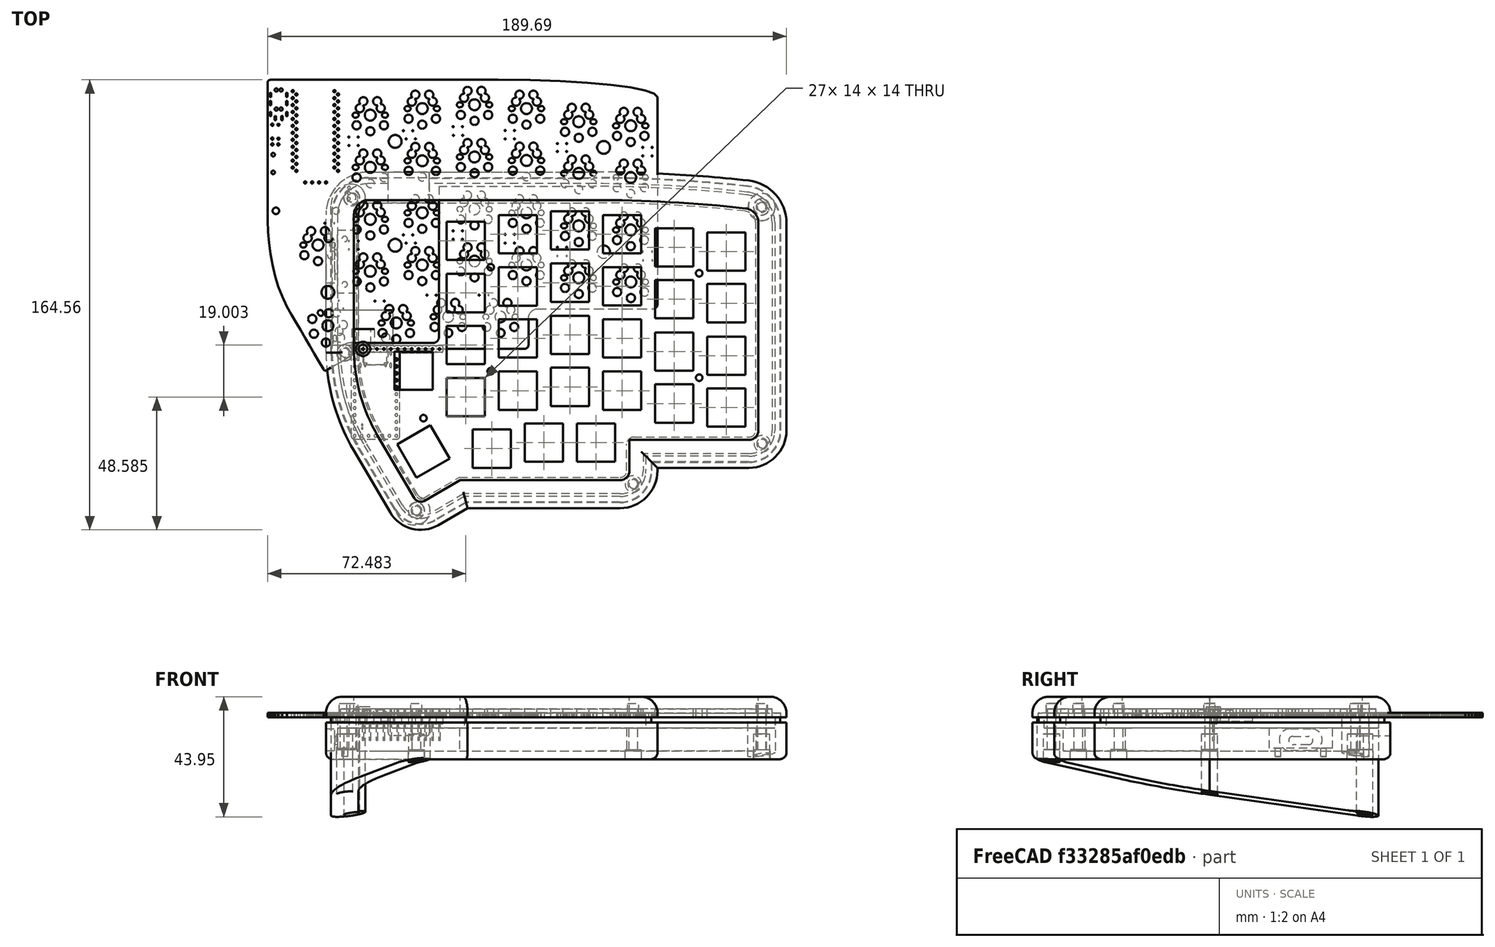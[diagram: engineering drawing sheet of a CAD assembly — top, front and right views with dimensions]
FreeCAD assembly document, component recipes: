
FREECAD ASSEMBLY — COMPONENT RECIPES ("pro_case_usbc_gasket_mount")

This assembly document has 10 components, labeled P0..P9 below (a component is one placed body or linked part). 8 of them carry a construction recipe — the FreeCAD feature program that regenerates the part from scratch, quoted from this document or its linked companion documents; the rest are supplied as boundary geometry only. No exploded tour is included for this assembly.
COMPONENT P0 — geometry summary ("Assembly"; no construction recipe available for this part):
  bounding box: 168.3 x 130.9 x 57.9 mm
  tessellated surface: 6,794 triangles
  volume: 358568995028408542041603690275402591667296508010351050356882624388695640748972656916483938942223122432 mm^3 (28139869802548311578441350783873821264969144354978867066293257606694140065651820190811947033165824% of its bounding box)
COMPONENT P1 — geometry summary ("lily58_pcb"; no construction recipe available for this part):
  bounding box: 142.5 x 106.3 x 1.6 mm
  tessellated surface: 11,472 triangles
  volume: 17508 mm^3 (72% of its bounding box)
  symmetry: mirror-symmetric across its z mid-plane
COMPONENT P2 — recipe-attached ("top_plate", modeled in this document).
Construction recipe (the document's own serialized feature program — sketch geometry with constraints, then the solid features built on it; lengths are millimeters unless a unit is written):

FEATURE [PartDesign::ShapeBinder] ShapeBinder002
  Placement = pos=(-82.9363,87.5957,1.6) rot=(0,0,1;0rad)
  Support = -> [Board_outline]
  TraceSupport = false
FEATURE [Sketcher::SketchObject] Sketch008  label="s_top_plate001"
  ExternalGeometry = -> [ShapeBinder002]
  FullyConstrained = true
  MapMode = 5
  Support = -> [XY_Plane010]
  expr: Constraints[435] = <<ss_top_plate>>.screw_hole_od
  expr: Constraints[85] = <<ss_top_plate>>.gasket_width
  sketch-geometry (187):
    g0: LineSegment StartX=27.7441 StartY=2.20222 StartZ=0 EndX=27.7441 EndY=50.2465 EndZ=0
    g1: LineSegment StartX=29.9578 StartY=52.4601 StartZ=0 EndX=84.3125 EndY=52.4601 EndZ=0
    g2: LineSegment StartX=142.522 StartY=46.1101 StartZ=0 EndX=142.522 EndY=-29.7428 EndZ=0
    g3: LineSegment StartX=95.381 StartY=-34.7428 StartZ=0 EndX=95.381 EndY=-44.4872 EndZ=0
    g4: LineSegment StartX=93.9034 StartY=-45.9648 StartZ=0 EndX=34.9248 EndY=-45.9648 EndZ=0
    g5: LineSegment StartX=34.9248 StartY=-45.9648 StartZ=0 EndX=21.3774 EndY=-53.8065 EndZ=0
    g6: LineSegment StartX=20.5079 StartY=-53.5776 StartZ=0 EndX=7.05497 EndY=-30.6854 EndZ=0
    g7: LineSegment StartX=98.881 StartY=-31.2428 StartZ=0 EndX=141.022 EndY=-31.2428 EndZ=0
    g8: LineSegment StartX=27.7441 StartY=2.20222 StartZ=0 EndX=2.19941 EndY=2.20233 EndZ=0
    g9: ArcOfCircle CenterX=59.4385 CenterY=0.0985715 CenterZ=0 NormalX=0 NormalY=0 NormalZ=1 AngleXU=0 Radius=60.7592 StartAngle=3.16603 EndAngle=3.67289
    g10: ArcOfCircle CenterX=2.19939 CenterY=-1.30071 CenterZ=0 NormalX=0 NormalY=0 NormalZ=1 AngleXU=0 Radius=3.50304 StartAngle=1.57079 EndAngle=3.16603
    g11: ArcOfCircle CenterX=84.3125 CenterY=-450.952 CenterZ=0 NormalX=0 NormalY=0 NormalZ=1 AngleXU=0 Radius=503.412 StartAngle=1.46083 EndAngle=1.5708
    g12: ArcOfCircle CenterX=139.192 CenterY=46.1101 CenterZ=0 NormalX=0 NormalY=0 NormalZ=1 AngleXU=0 Radius=3.32961 StartAngle=6e-16 EndAngle=1.46083
    g13: ArcOfCircle CenterX=21.0579 CenterY=-53.2544 CenterZ=0 NormalX=0 NormalY=0 NormalZ=1 AngleXU=0 Radius=0.637877 StartAngle=3.67289 EndAngle=5.2371
    g14: ArcOfCircle CenterX=93.9034 CenterY=-44.4872 CenterZ=0 NormalX=0 NormalY=0 NormalZ=1 AngleXU=0 Radius=1.47761 StartAngle=4.71239 EndAngle=6.28319
    g15: ArcOfCircle CenterX=98.881 CenterY=-34.7428 CenterZ=0 NormalX=0 NormalY=0 NormalZ=1 AngleXU=0 Radius=3.5 StartAngle=1.5708 EndAngle=3.14159
    g16: ArcOfCircle CenterX=141.022 CenterY=-29.7428 CenterZ=0 NormalX=0 NormalY=0 NormalZ=1 AngleXU=0 Radius=1.5 StartAngle=4.71239 EndAngle=6.28319
    g17: ArcOfCircle CenterX=29.9578 CenterY=50.2465 CenterZ=0 NormalX=0 NormalY=0 NormalZ=1 AngleXU=0 Radius=2.21364 StartAngle=1.5708 EndAngle=3.14159
    g18: LineSegment StartX=-1.3026 StartY=-1.38632 StartZ=0 EndX=0.0777 EndY=-1.38632 EndZ=0
    g19: LineSegment StartX=27.7344 StartY=59.4601 StartZ=0 EndX=84.3125 EndY=59.4601 EndZ=0
    g20: LineSegment StartX=149.522 StartY=46.1101 StartZ=0 EndX=149.522 EndY=-29.7428 EndZ=0
    g21: LineSegment StartX=141.022 StartY=-38.2428 StartZ=0 EndX=102.381 EndY=-38.2428 EndZ=0
    g22: LineSegment StartX=102.381 StartY=-38.2428 StartZ=0 EndX=102.381 EndY=-44.4872 EndZ=0
    g23: LineSegment StartX=93.9034 StartY=-52.9648 StartZ=0 EndX=36.8046 EndY=-52.9648 EndZ=0
    g24: LineSegment StartX=36.8046 StartY=-52.9648 StartZ=0 EndX=24.8842 EndY=-59.8648 EndZ=0
    g25: LineSegment StartX=14.4729 StartY=-57.1242 StartZ=0 EndX=1.01993 EndY=-34.232 EndZ=0
    g26: ArcOfCircle CenterX=139.192 CenterY=46.1101 CenterZ=0 NormalX=0 NormalY=0 NormalZ=1 AngleXU=0 Radius=10.3296 StartAngle=0 EndAngle=1.46083
    g27: ArcOfCircle CenterX=84.3125 CenterY=-450.952 CenterZ=0 NormalX=0 NormalY=0 NormalZ=1 AngleXU=0 Radius=510.412 StartAngle=1.46083 EndAngle=1.5708
    g28: ArcOfCircle CenterX=59.4385 CenterY=0.0985715 CenterZ=0 NormalX=0 NormalY=0 NormalZ=1 AngleXU=0 Radius=67.7592 StartAngle=3.16351 EndAngle=3.67289
    g29: ArcOfCircle CenterX=21.0579 CenterY=-53.2544 CenterZ=0 NormalX=0 NormalY=0 NormalZ=1 AngleXU=0 Radius=7.63788 StartAngle=3.67289 EndAngle=5.2371
    g30: ArcOfCircle CenterX=93.9034 CenterY=-44.4872 CenterZ=0 NormalX=0 NormalY=0 NormalZ=1 AngleXU=0 Radius=8.47761 StartAngle=4.71239 EndAngle=6.28319
    g31: ArcOfCircle CenterX=141.022 CenterY=-29.7428 CenterZ=0 NormalX=0 NormalY=0 NormalZ=1 AngleXU=0 Radius=8.5 StartAngle=4.71239 EndAngle=6.28319
    g32: LineSegment StartX=141.022 StartY=-38.2428 StartZ=0 EndX=141.022 EndY=-31.2428 EndZ=0
    g33: LineSegment StartX=93.9034 StartY=-52.9648 StartZ=0 EndX=93.9034 EndY=-45.9648 EndZ=0
    g34: LineSegment StartX=24.8842 StartY=-59.8648 StartZ=0 EndX=21.3774 EndY=-53.8065 EndZ=0
    g35: LineSegment StartX=1.01993 StartY=-34.232 StartZ=0 EndX=7.05497 EndY=-30.6854 EndZ=0
    g36: LineSegment StartX=27.7344 StartY=59.4601 StartZ=0 EndX=27.7441 EndY=4.40223 EndZ=0
    g37: LineSegment StartX=25.5445 StartY=2.20223 StartZ=0 EndX=-4.79372 EndY=2.20223 EndZ=0
    g38: ArcOfCircle CenterX=-4.79372 CenterY=-1.30937 CenterZ=0 NormalX=0 NormalY=0 NormalZ=1 AngleXU=0 Radius=3.5116 StartAngle=1.5708 EndAngle=3.16351
    g39: ArcOfCircle CenterX=25.5445 CenterY=4.40184 CenterZ=0 NormalX=0 NormalY=0 NormalZ=1 AngleXU=0 Radius=2.19961 StartAngle=4.71239 EndAngle=6.28336
    g40: LineSegment StartX=84.3125 StartY=52.4601 StartZ=0 EndX=84.3125 EndY=59.4601 EndZ=0
    g41: LineSegment StartX=11.463 StartY=-0.95364 StartZ=0 EndX=25.4152 EndY=-0.95364 EndZ=0
    g42: LineSegment StartX=25.4152 StartY=-0.95364 StartZ=0 EndX=25.4152 EndY=-14.9537 EndZ=0
    g43: LineSegment StartX=25.4152 StartY=-14.9537 StartZ=0 EndX=11.463 EndY=-14.9537 EndZ=0
    g44: LineSegment StartX=11.463 StartY=-14.9537 StartZ=0 EndX=11.463 EndY=-0.95364 EndZ=0
    g45: LineSegment StartX=30.5626 StartY=46.5466 StartZ=0 EndX=44.5628 EndY=46.5466 EndZ=0
    g46: LineSegment StartX=44.5628 StartY=46.5466 StartZ=0 EndX=44.5628 EndY=32.5466 EndZ=0
    g47: LineSegment StartX=44.5628 StartY=32.5466 StartZ=0 EndX=30.5626 EndY=32.5466 EndZ=0
    g48: LineSegment StartX=30.5626 StartY=32.5466 StartZ=0 EndX=30.5626 EndY=46.5466 EndZ=0
    g49: LineSegment StartX=49.5629 StartY=48.9469 StartZ=0 EndX=63.5631 EndY=48.9469 EndZ=0
    g50: LineSegment StartX=63.5631 StartY=48.9469 StartZ=0 EndX=63.5631 EndY=34.9469 EndZ=0
    g51: LineSegment StartX=63.5631 StartY=34.9469 StartZ=0 EndX=49.5629 EndY=34.9469 EndZ=0
    g52: LineSegment StartX=49.5629 StartY=34.9469 StartZ=0 EndX=49.5629 EndY=48.9469 EndZ=0
    g53: LineSegment StartX=68.5928 StartY=50.3363 StartZ=0 EndX=82.593 EndY=50.3363 EndZ=0
    g54: LineSegment StartX=82.593 StartY=50.3363 StartZ=0 EndX=82.593 EndY=36.3362 EndZ=0
    g55: LineSegment StartX=82.593 StartY=36.3362 StartZ=0 EndX=68.5928 EndY=36.3362 EndZ=0
    g56: LineSegment StartX=68.5928 StartY=36.3362 StartZ=0 EndX=68.5928 EndY=50.3363 EndZ=0
    g57: LineSegment StartX=87.6676 StartY=48.9469 StartZ=0 EndX=101.668 EndY=48.9469 EndZ=0
    g58: LineSegment StartX=101.668 StartY=48.9469 StartZ=0 EndX=101.668 EndY=34.9469 EndZ=0
    g59: LineSegment StartX=101.668 StartY=34.9469 StartZ=0 EndX=87.6676 EndY=34.9469 EndZ=0
    g60: LineSegment StartX=87.6676 StartY=34.9469 StartZ=0 EndX=87.6676 EndY=48.9469 EndZ=0
    g61: LineSegment StartX=106.764 StartY=44.1463 StartZ=0 EndX=120.764 EndY=44.1463 EndZ=0
    g62: LineSegment StartX=120.764 StartY=44.1463 StartZ=0 EndX=120.764 EndY=30.1463 EndZ=0
    g63: LineSegment StartX=120.764 StartY=30.1463 StartZ=0 EndX=106.764 EndY=30.1463 EndZ=0
    g64: LineSegment StartX=106.764 StartY=30.1463 StartZ=0 EndX=106.764 EndY=44.1463 EndZ=0
    g65: LineSegment StartX=125.761 StartY=42.6469 StartZ=0 EndX=139.762 EndY=42.6469 EndZ=0
    g66: LineSegment StartX=139.762 StartY=42.6469 StartZ=0 EndX=139.762 EndY=28.6464 EndZ=0
    g67: LineSegment StartX=139.762 StartY=28.6464 StartZ=0 EndX=125.761 EndY=28.6464 EndZ=0
    g68: LineSegment StartX=125.761 StartY=28.6464 StartZ=0 EndX=125.761 EndY=42.6469 EndZ=0
    g69: LineSegment StartX=30.5636 StartY=27.4453 StartZ=0 EndX=44.5638 EndY=27.4453 EndZ=0
    g70: LineSegment StartX=44.5638 StartY=27.4453 StartZ=0 EndX=44.5638 EndY=13.4453 EndZ=0
    g71: LineSegment StartX=44.5638 StartY=13.4453 StartZ=0 EndX=30.5636 EndY=13.4453 EndZ=0
    g72: LineSegment StartX=30.5636 StartY=13.4453 StartZ=0 EndX=30.5636 EndY=27.4453 EndZ=0
    g73: LineSegment StartX=49.5629 StartY=29.8461 StartZ=0 EndX=63.5631 EndY=29.8461 EndZ=0
    g74: LineSegment StartX=63.5631 StartY=29.8461 StartZ=0 EndX=63.5631 EndY=15.8461 EndZ=0
    g75: LineSegment StartX=63.5631 StartY=15.8461 StartZ=0 EndX=49.5629 EndY=15.8461 EndZ=0
    g76: LineSegment StartX=49.5629 StartY=15.8461 StartZ=0 EndX=49.5629 EndY=29.8461 EndZ=0
    g77: LineSegment StartX=68.6637 StartY=31.2457 StartZ=0 EndX=82.6639 EndY=31.2457 EndZ=0
    g78: LineSegment StartX=82.6639 StartY=31.2457 StartZ=0 EndX=82.6639 EndY=17.2456 EndZ=0
    g79: LineSegment StartX=82.6639 StartY=17.2456 StartZ=0 EndX=68.6637 EndY=17.2456 EndZ=0
    g80: LineSegment StartX=68.6637 StartY=17.2456 StartZ=0 EndX=68.6637 EndY=31.2457 EndZ=0
    g81: LineSegment StartX=87.6617 StartY=29.9467 StartZ=0 EndX=101.662 EndY=29.9467 EndZ=0
    g82: LineSegment StartX=101.662 StartY=29.9467 StartZ=0 EndX=101.662 EndY=15.9466 EndZ=0
    g83: LineSegment StartX=101.662 StartY=15.9466 StartZ=0 EndX=87.6617 EndY=15.9466 EndZ=0
    g84: LineSegment StartX=87.6617 StartY=15.9466 StartZ=0 EndX=87.6617 EndY=29.9467 EndZ=0
    g85: LineSegment StartX=106.762 StartY=25.2462 StartZ=0 EndX=120.763 EndY=25.2462 EndZ=0
    g86: LineSegment StartX=120.763 StartY=25.2462 StartZ=0 EndX=120.763 EndY=11.2462 EndZ=0
    g87: LineSegment StartX=120.763 StartY=11.2462 StartZ=0 EndX=106.762 EndY=11.2462 EndZ=0
    g88: LineSegment StartX=106.762 StartY=11.2462 StartZ=0 EndX=106.762 EndY=25.2462 EndZ=0
    g89: LineSegment StartX=125.761 StartY=23.7455 StartZ=0 EndX=139.762 EndY=23.7455 EndZ=0
    g90: LineSegment StartX=139.762 StartY=23.7455 StartZ=0 EndX=139.762 EndY=9.74756 EndZ=0
    g91: LineSegment StartX=139.762 StartY=9.74756 StartZ=0 EndX=125.761 EndY=9.74756 EndZ=0
    g92: LineSegment StartX=125.761 StartY=9.74756 StartZ=0 EndX=125.761 EndY=23.7455 EndZ=0
    g93: LineSegment StartX=30.5626 StartY=8.44811 StartZ=0 EndX=44.5628 EndY=8.44811 EndZ=0
    g94: LineSegment StartX=44.5628 StartY=8.44811 StartZ=0 EndX=44.5628 EndY=-5.55192 EndZ=0
    g95: LineSegment StartX=44.5628 StartY=-5.55192 StartZ=0 EndX=30.5626 EndY=-5.55192 EndZ=0
    g96: LineSegment StartX=30.5626 StartY=-5.55192 StartZ=0 EndX=30.5626 EndY=8.44811 EndZ=0
    g97: LineSegment StartX=49.5638 StartY=10.8451 StartZ=0 EndX=63.564 EndY=10.8451 EndZ=0
    g98: LineSegment StartX=63.564 StartY=10.8451 StartZ=0 EndX=63.564 EndY=-3.15488 EndZ=0
    g99: LineSegment StartX=63.564 StartY=-3.15488 StartZ=0 EndX=49.5638 EndY=-3.15488 EndZ=0
    g100: LineSegment StartX=49.5638 StartY=-3.15488 StartZ=0 EndX=49.5638 EndY=10.8451 EndZ=0
    g101: LineSegment StartX=68.6637 StartY=12.1474 StartZ=0 EndX=82.6639 EndY=12.1474 EndZ=0
    g102: LineSegment StartX=82.6639 StartY=12.1474 StartZ=0 EndX=82.6639 EndY=-1.85258 EndZ=0
    g103: LineSegment StartX=82.6639 StartY=-1.85258 StartZ=0 EndX=68.6637 EndY=-1.85258 EndZ=0
    g104: LineSegment StartX=68.6637 StartY=-1.85258 StartZ=0 EndX=68.6637 EndY=12.1474 EndZ=0
    g105: LineSegment StartX=87.6637 StartY=10.8474 StartZ=0 EndX=101.664 EndY=10.8474 EndZ=0
    g106: LineSegment StartX=101.664 StartY=10.8474 StartZ=0 EndX=101.664 EndY=-3.15263 EndZ=0
    g107: LineSegment StartX=101.664 StartY=-3.15263 StartZ=0 EndX=87.6637 EndY=-3.15263 EndZ=0
    g108: LineSegment StartX=87.6637 StartY=-3.15263 StartZ=0 EndX=87.6637 EndY=10.8474 EndZ=0
    g109: LineSegment StartX=106.749 StartY=6.04637 StartZ=0 EndX=120.749 EndY=6.04637 EndZ=0
    g110: LineSegment StartX=120.749 StartY=6.04637 StartZ=0 EndX=120.749 EndY=-7.95365 EndZ=0
    g111: LineSegment StartX=120.749 StartY=-7.95365 StartZ=0 EndX=106.749 EndY=-7.95365 EndZ=0
    g112: LineSegment StartX=106.749 StartY=-7.95365 StartZ=0 EndX=106.749 EndY=6.04637 EndZ=0
    g113: LineSegment StartX=125.764 StartY=4.54519 StartZ=0 EndX=139.764 EndY=4.54519 EndZ=0
    g114: LineSegment StartX=139.764 StartY=4.54519 StartZ=0 EndX=139.764 EndY=-9.45483 EndZ=0
    g115: LineSegment StartX=139.764 StartY=-9.45483 StartZ=0 EndX=125.764 EndY=-9.45483 EndZ=0
    g116: LineSegment StartX=125.764 StartY=-9.45483 StartZ=0 EndX=125.764 EndY=4.54519 EndZ=0
    g117: LineSegment StartX=30.5626 StartY=-10.5548 StartZ=0 EndX=44.5628 EndY=-10.5548 EndZ=0
    g118: LineSegment StartX=44.5628 StartY=-10.5548 StartZ=0 EndX=44.5628 EndY=-24.5548 EndZ=0
    g119: LineSegment StartX=44.5628 StartY=-24.5548 StartZ=0 EndX=30.5626 EndY=-24.5548 EndZ=0
    g120: LineSegment StartX=30.5626 StartY=-24.5548 StartZ=0 EndX=30.5626 EndY=-10.5548 EndZ=0
    g121: LineSegment StartX=49.5638 StartY=-8.25337 StartZ=0 EndX=63.564 EndY=-8.25337 EndZ=0
    g122: LineSegment StartX=63.564 StartY=-8.25337 StartZ=0 EndX=63.564 EndY=-22.2534 EndZ=0
    g123: LineSegment StartX=63.564 StartY=-22.2534 StartZ=0 EndX=49.5638 EndY=-22.2534 EndZ=0
    g124: LineSegment StartX=49.5638 StartY=-22.2534 StartZ=0 EndX=49.5638 EndY=-8.25337 EndZ=0
    g125: LineSegment StartX=68.6625 StartY=-6.85278 StartZ=0 EndX=82.6627 EndY=-6.85278 EndZ=0
    g126: LineSegment StartX=82.6627 StartY=-6.85278 StartZ=0 EndX=82.6627 EndY=-20.8528 EndZ=0
    g127: LineSegment StartX=82.6627 StartY=-20.8528 StartZ=0 EndX=68.6625 EndY=-20.8528 EndZ=0
    g128: LineSegment StartX=68.6625 StartY=-20.8528 StartZ=0 EndX=68.6625 EndY=-6.85278 EndZ=0
    g129: LineSegment StartX=87.663 StartY=-8.25358 StartZ=0 EndX=101.663 EndY=-8.25358 EndZ=0
    g130: LineSegment StartX=101.663 StartY=-8.25358 StartZ=0 EndX=101.663 EndY=-22.2536 EndZ=0
    g131: LineSegment StartX=101.663 StartY=-22.2536 StartZ=0 EndX=87.663 EndY=-22.2536 EndZ=0
    g132: LineSegment StartX=87.663 StartY=-22.2536 StartZ=0 EndX=87.663 EndY=-8.25358 EndZ=0
    g133: LineSegment StartX=106.763 StartY=-12.9526 StartZ=0 EndX=120.764 EndY=-12.9526 EndZ=0
    g134: LineSegment StartX=120.764 StartY=-12.9526 StartZ=0 EndX=120.764 EndY=-26.9526 EndZ=0
    g135: LineSegment StartX=120.764 StartY=-26.9526 StartZ=0 EndX=106.763 EndY=-26.9526 EndZ=0
    g136: LineSegment StartX=106.763 StartY=-26.9526 StartZ=0 EndX=106.763 EndY=-12.9526 EndZ=0
    g137: LineSegment StartX=125.812 StartY=-14.4535 StartZ=0 EndX=139.813 EndY=-14.4535 EndZ=0
    g138: LineSegment StartX=139.813 StartY=-14.4535 StartZ=0 EndX=139.813 EndY=-28.4535 EndZ=0
    g139: LineSegment StartX=139.813 StartY=-28.4535 StartZ=0 EndX=125.812 EndY=-28.4535 EndZ=0
    g140: LineSegment StartX=125.812 StartY=-28.4535 StartZ=0 EndX=125.812 EndY=-14.4535 EndZ=0
    g141: LineSegment StartX=40.0622 StartY=-29.4536 StartZ=0 EndX=54.0624 EndY=-29.4536 EndZ=0
    g142: LineSegment StartX=54.0624 StartY=-29.4536 StartZ=0 EndX=54.0624 EndY=-43.4537 EndZ=0
    g143: LineSegment StartX=54.0624 StartY=-43.4537 StartZ=0 EndX=40.0622 EndY=-43.4537 EndZ=0
    g144: LineSegment StartX=40.0622 StartY=-43.4537 StartZ=0 EndX=40.0622 EndY=-29.4536 EndZ=0
    g145: LineSegment StartX=59.0628 StartY=-27.2032 StartZ=0 EndX=73.063 EndY=-27.2032 EndZ=0
    g146: LineSegment StartX=73.063 StartY=-27.2032 StartZ=0 EndX=73.063 EndY=-41.2032 EndZ=0
    g147: LineSegment StartX=73.063 StartY=-41.2032 StartZ=0 EndX=59.0628 EndY=-41.2032 EndZ=0
    g148: LineSegment StartX=59.0628 StartY=-41.2032 StartZ=0 EndX=59.0628 EndY=-27.2032 EndZ=0
    g149: LineSegment StartX=78.1633 StartY=-27.2043 StartZ=0 EndX=92.1637 EndY=-27.2043 EndZ=0
    g150: LineSegment StartX=92.1637 StartY=-27.2043 StartZ=0 EndX=92.1637 EndY=-41.2047 EndZ=0
    g151: LineSegment StartX=92.1637 StartY=-41.2047 StartZ=0 EndX=78.1633 EndY=-41.2047 EndZ=0
    g152: LineSegment StartX=78.1633 StartY=-41.2047 StartZ=0 EndX=78.1633 EndY=-27.2043 EndZ=0
    g153: LineSegment StartX=12.5009 StartY=-34.891 StartZ=0 EndX=24.6255 EndY=-27.8909 EndZ=0
    g154: LineSegment StartX=24.6255 StartY=-27.8909 StartZ=0 EndX=31.6255 EndY=-40.0153 EndZ=0
    g155: LineSegment StartX=31.6255 StartY=-40.0153 StartZ=0 EndX=19.501 EndY=-47.0154 EndZ=0
    g156: LineSegment StartX=19.501 StartY=-47.0154 StartZ=0 EndX=12.5009 EndY=-34.891 EndZ=0
    g157: Circle CenterX=46.6637 CenterY=29.8957 CenterZ=0 NormalX=0 NormalY=0 NormalZ=1 AngleXU=0 Radius=1.2
    g158: Circle CenterX=122.864 CenterY=27.6957 CenterZ=0 NormalX=0 NormalY=0 NormalZ=1 AngleXU=0 Radius=1.2
    g159: Circle CenterX=122.864 CenterY=-10.5043 CenterZ=0 NormalX=0 NormalY=0 NormalZ=1 AngleXU=0 Radius=1.2
    g160: Circle CenterX=46.6637 CenterY=-8.10427 CenterZ=0 NormalX=0 NormalY=0 NormalZ=1 AngleXU=0 Radius=1.2
    g161: Circle CenterX=22.0637 CenterY=-25.3043 CenterZ=0 NormalX=0 NormalY=0 NormalZ=1 AngleXU=0 Radius=1.2
    g162: Circle CenterX=145.695 CenterY=51.9344 CenterZ=0 NormalX=0 NormalY=0 NormalZ=1 AngleXU=0 Radius=1.6
    g163: Circle CenterX=145.901 CenterY=-34.6219 CenterZ=0 NormalX=0 NormalY=0 NormalZ=1 AngleXU=0 Radius=1.6
    g164: Circle CenterX=98.7666 CenterY=-49.3504 CenterZ=0 NormalX=0 NormalY=0 NormalZ=1 AngleXU=0 Radius=1.6
    g165: Circle CenterX=19.5209 CenterY=-59.0934 CenterZ=0 NormalX=0 NormalY=0 NormalZ=1 AngleXU=0 Radius=1.6
    g166: Circle CenterX=-6.70447 CenterY=-1.38632 CenterZ=0 NormalX=0 NormalY=0 NormalZ=1 AngleXU=0 Radius=1.6
    g167: LineSegment StartX=20.8955 StartY=-53.8713 StartZ=0 EndX=19.1136 EndY=-60.6407 EndZ=0
    g168: LineSegment StartX=19.1136 StartY=-60.6407 StartZ=0 EndX=24.8842 EndY=-59.8648 EndZ=0
    g169: LineSegment StartX=19.1136 StartY=-60.6407 StartZ=0 EndX=14.4729 EndY=-57.1242 EndZ=0
    g170: LineSegment StartX=20.5079 StartY=-53.5776 StartZ=0 EndX=20.8955 EndY=-53.8713 EndZ=0
    g171: LineSegment StartX=21.3774 StartY=-53.8065 StartZ=0 EndX=20.8955 EndY=-53.8713 EndZ=0
    g172: LineSegment StartX=94.9482 StartY=-45.532 StartZ=0 EndX=99.8979 EndY=-50.4817 EndZ=0
    g173: LineSegment StartX=94.9482 StartY=-45.532 StartZ=0 EndX=93.9034 EndY=-44.4872 EndZ=0
    g174: LineSegment StartX=93.9034 StartY=-52.9648 StartZ=0 EndX=99.8979 EndY=-50.4817 EndZ=0
    g175: LineSegment StartX=99.8979 StartY=-50.4817 StartZ=0 EndX=102.381 EndY=-44.4872 EndZ=0
    g176: LineSegment StartX=142.082 StartY=-30.8035 StartZ=0 EndX=147.032 EndY=-35.7533 EndZ=0
    g177: LineSegment StartX=141.022 StartY=-38.2428 StartZ=0 EndX=147.032 EndY=-35.7533 EndZ=0
    g178: LineSegment StartX=147.032 StartY=-35.7533 StartZ=0 EndX=149.522 EndY=-29.7428 EndZ=0
    g179: LineSegment StartX=141.022 StartY=-31.2428 StartZ=0 EndX=142.082 EndY=-30.8035 EndZ=0
    g180: LineSegment StartX=142.082 StartY=-30.8035 StartZ=0 EndX=142.522 EndY=-29.7428 EndZ=0
    g181: LineSegment StartX=141.672 StartY=48.3316 StartZ=0 EndX=146.887 EndY=53.0018 EndZ=0
    g182: LineSegment StartX=140.326 StartY=56.3773 StartZ=0 EndX=146.887 EndY=53.0018 EndZ=0
    g183: LineSegment StartX=146.887 StartY=53.0018 StartZ=0 EndX=149.522 EndY=46.1101 EndZ=0
    g184: LineSegment StartX=142.522 StartY=46.1101 StartZ=0 EndX=141.672 EndY=48.3316 EndZ=0
    g185: LineSegment StartX=141.672 StartY=48.3316 StartZ=0 EndX=139.557 EndY=49.4196 EndZ=0
    g186: LineSegment StartX=-1.3026 StartY=-1.38632 StartZ=0 EndX=-8.30447 EndY=-1.38632 EndZ=0
  constraints (448):
    c: Vertical(g0)
    c: Coincident(g1,g-3)
    c: Horizontal(g1)
    c: Vertical(g2)
    c: Coincident(g4,g-8)
    c: Coincident(g4,g5)
    c: Coincident(g6,g-9)
    c: PointOnObject(g-8,g5)
    c: PointOnObject(g-7,g4)
    c: Horizontal(g7)
    c: Coincident(g8,g0)
    c: Tangent(g9,g6) = 1.5708
    c: Tangent(g9,g10) = -1.5708
    c: Tangent(g8,g10) = -1.5708
    c: Tangent(g11,g1) = 1.5708
    c: PointOnObject(g-13,g11)
    c: Tangent(g11,g12) = -1.5708
    c: Tangent(g2,g12) = 1.5708
    c: Coincident(g2,g-4)
    c: Tangent(g5,g13) = 1.5708
    c: Tangent(g6,g13) = 1.5708
    c: Coincident(g6,g-9)
    c: Tangent(g4,g14) = 1.5708
    c: Tangent(g3,g14) = 1.5708
    c: Tangent(g3,g15) = -1.5708
    c: Tangent(g7,g15) = 1.5708
    c: Tangent(g7,g16) = -1.5708
    c: Tangent(g2,g16) = 1.5708
    c: Coincident(g7,g-5)
    c: Coincident(g3,g-6)
    c: Coincident(g3,g-6)
    c: Coincident(g8,g-10)
    c: Tangent(g0,g17) = 1.5708
    c: Tangent(g1,g17) = 1.5708
    c: Coincident(g0,g-11)
    c: Coincident(g18,g9)
    c: Coincident(g18,g-12)
    c: Horizontal(g18)
    c: Horizontal(g19)
    c: Vertical(g20)
    c: Horizontal(g21)
    c: Coincident(g21,g22)
    c: Vertical(g22)
    c: Horizontal(g23)
    c: Coincident(g23,g24)
    c: Coincident(g27,g11)
    c: Tangent(g27,g19) = 1.5708
    c: Tangent(g27,g26) = -1.5708
    c: Tangent(g26,g20) = 1.5708
    c: Coincident(g28,g9)
    c: Coincident(g28,g25)
    c: Tangent(g25,g29) = 1.5708
    c: Tangent(g24,g29) = 1.5708
    c: Tangent(g23,g30) = 1.5708
    c: Tangent(g22,g30) = 1.5708
    c: Tangent(g21,g31) = 1.5708
    c: Tangent(g20,g31) = 1.5708
    c: Coincident(g31,g16)
    c: Coincident(g26,g12)
    c: Coincident(g29,g13)
    c: Parallel(g24,g5)
    c: Parallel(g6,g25)
    c: Coincident(g30,g14)
    c: Coincident(g32,g21)
    c: Coincident(g32,g7)
    c: Coincident(g33,g23)
    c: Coincident(g33,g4)
    c: Coincident(g34,g24)
    c: Coincident(g34,g5)
    c: Coincident(g35,g25)
    c: Coincident(g35,g6)
    c: Perpendicular(g6,g35)
    c: Coincident(g36,g19)
    c: Horizontal(g37)
    c: Tangent(g28,g38) = -1.5708
    c: Tangent(g37,g38) = -1.5708
    c: Horizontal(g28,g9)
    c: Tangent(g36,g39) = 1.5708
    c: Tangent(g37,g39) = 1.5708
    c: Coincident(g37,g-10)
    c: Coincident(g36,g-11)
    c: Coincident(g40,g1)
    c: Coincident(g40,g19)
    c: Equal(g32,g33)
    c: Equal(g33,g34)
    c: DistanceY(g40,g40) = 7
    c: PointOnObject(g37,g8)
    c: Coincident(g41,g42)
    c: Coincident(g42,g43)
    c: Coincident(g43,g44)
    c: Coincident(g44,g41)
    c: Horizontal(g41)
    c: Horizontal(g43)
    c: Vertical(g42)
    c: Vertical(g44)
    c: Coincident(g41,g-16)
    c: Coincident(g42,g-17)
    c: Coincident(g45,g46)
    c: Coincident(g46,g47)
    c: Coincident(g47,g48)
    c: Coincident(g48,g45)
    c: Horizontal(g45)
    c: Horizontal(g47)
    c: Vertical(g46)
    c: Vertical(g48)
    c: Coincident(g45,g-18)
    c: Coincident(g46,g-19)
    c: Coincident(g49,g50)
    c: Coincident(g50,g51)
    c: Coincident(g51,g52)
    c: Coincident(g52,g49)
    c: Horizontal(g49)
    c: Horizontal(g51)
    c: Vertical(g50)
    c: Vertical(g52)
    c: Coincident(g49,g-20)
    c: Coincident(g50,g-21)
    c: Coincident(g53,g54)
    c: Coincident(g54,g55)
    c: Coincident(g55,g56)
    c: Coincident(g56,g53)
    c: Horizontal(g53)
    c: Horizontal(g55)
    c: Vertical(g54)
    c: Vertical(g56)
    c: Coincident(g53,g-22)
    c: Coincident(g54,g-23)
    c: Coincident(g57,g58)
    c: Coincident(g58,g59)
    c: Coincident(g59,g60)
    c: Coincident(g60,g57)
    c: Horizontal(g57)
    c: Horizontal(g59)
    c: Vertical(g58)
    c: Vertical(g60)
    c: Coincident(g57,g-24)
    c: Coincident(g58,g-25)
    c: Coincident(g61,g62)
    c: Coincident(g62,g63)
    c: Coincident(g63,g64)
    c: Coincident(g64,g61)
    c: Horizontal(g61)
    c: Horizontal(g63)
    c: Vertical(g62)
    c: Vertical(g64)
    c: Coincident(g61,g-26)
    c: Coincident(g62,g-27)
    c: Coincident(g65,g66)
    c: Coincident(g66,g67)
    c: Coincident(g67,g68)
    c: Coincident(g68,g65)
    c: Horizontal(g65)
    c: Horizontal(g67)
    c: Vertical(g66)
    c: Vertical(g68)
    c: Coincident(g65,g-28)
    c: Coincident(g66,g-29)
    c: Coincident(g69,g70)
    c: Coincident(g70,g71)
    c: Coincident(g71,g72)
    c: Coincident(g72,g69)
    c: Horizontal(g69)
    c: Horizontal(g71)
    c: Vertical(g70)
    c: Vertical(g72)
    c: Coincident(g69,g-40)
    c: Coincident(g70,g-41)
    c: Coincident(g73,g74)
    c: Coincident(g74,g75)
    c: Coincident(g75,g76)
    c: Coincident(g76,g73)
    c: Horizontal(g73)
    c: Horizontal(g75)
    c: Vertical(g74)
    c: Vertical(g76)
    c: Coincident(g73,g-38)
    c: Coincident(g74,g-39)
    c: Coincident(g77,g78)
    c: Coincident(g78,g79)
    c: Coincident(g79,g80)
    c: Coincident(g80,g77)
    c: Horizontal(g77)
    c: Horizontal(g79)
    c: Vertical(g78)
    c: Vertical(g80)
    c: Coincident(g77,g-37)
    c: Coincident(g78,g-36)
    c: Coincident(g81,g82)
    c: Coincident(g82,g83)
    c: Coincident(g83,g84)
    c: Coincident(g84,g81)
    c: Horizontal(g81)
    c: Horizontal(g83)
    c: Vertical(g82)
    c: Vertical(g84)
    c: Coincident(g81,g-34)
    c: Coincident(g82,g-35)
    c: Coincident(g85,g86)
    c: Coincident(g86,g87)
    c: Coincident(g87,g88)
    c: Coincident(g88,g85)
    c: Horizontal(g85)
    c: Horizontal(g87)
    c: Vertical(g86)
    c: Vertical(g88)
    c: Coincident(g85,g-33)
    c: Coincident(g86,g-32)
    c: Coincident(g89,g90)
    c: Coincident(g90,g91)
    c: Coincident(g91,g92)
    c: Coincident(g92,g89)
    c: Horizontal(g89)
    c: Horizontal(g91)
    c: Vertical(g90)
    c: Vertical(g92)
    c: Coincident(g89,g-30)
    c: Coincident(g90,g-31)
    c: Coincident(g93,g94)
    c: Coincident(g94,g95)
    c: Coincident(g95,g96)
    c: Coincident(g96,g93)
    c: Horizontal(g93)
    c: Horizontal(g95)
    c: Vertical(g94)
    c: Vertical(g96)
    c: Coincident(g93,g-45)
    c: Coincident(g94,g-44)
    c: Coincident(g97,g98)
    c: Coincident(g98,g99)
    c: Coincident(g99,g100)
    c: Coincident(g100,g97)
    c: Horizontal(g97)
    c: Horizontal(g99)
    c: Vertical(g98)
    c: Vertical(g100)
    c: Coincident(g97,g-46)
    c: Coincident(g98,g-48)
    c: Coincident(g101,g102)
    c: Coincident(g102,g103)
    c: Coincident(g103,g104)
    c: Coincident(g104,g101)
    c: Horizontal(g101)
    c: Horizontal(g103)
    c: Vertical(g102)
    c: Vertical(g104)
    c: Coincident(g101,g-47)
    c: Coincident(g102,g-49)
    c: Coincident(g105,g106)
    c: Coincident(g106,g107)
    c: Coincident(g107,g108)
    c: Coincident(g108,g105)
    c: Horizontal(g105)
    c: Horizontal(g107)
    c: Vertical(g106)
    c: Vertical(g108)
    c: Coincident(g105,g-50)
    c: Coincident(g106,g-51)
    c: Coincident(g109,g110)
    c: Coincident(g110,g111)
    c: Coincident(g111,g112)
    c: Coincident(g112,g109)
    c: Horizontal(g109)
    c: Horizontal(g111)
    c: Vertical(g110)
    c: Vertical(g112)
    c: Coincident(g109,g-52)
    c: Coincident(g110,g-53)
    c: Coincident(g113,g114)
    c: Coincident(g114,g115)
    c: Coincident(g115,g116)
    c: Coincident(g116,g113)
    c: Horizontal(g113)
    c: Horizontal(g115)
    c: Vertical(g114)
    c: Vertical(g116)
    c: Coincident(g113,g-54)
    c: Coincident(g114,g-55)
    c: Coincident(g117,g118)
    c: Coincident(g118,g119)
    c: Coincident(g119,g120)
    c: Coincident(g120,g117)
    c: Horizontal(g117)
    c: Horizontal(g119)
    c: Vertical(g118)
    c: Vertical(g120)
    c: Coincident(g117,g-66)
    c: Coincident(g118,g-67)
    c: Coincident(g121,g122)
    c: Coincident(g122,g123)
    c: Coincident(g123,g124)
    c: Coincident(g124,g121)
    c: Horizontal(g121)
    c: Horizontal(g123)
    c: Vertical(g122)
    c: Vertical(g124)
    c: Coincident(g121,g-64)
    c: Coincident(g122,g-65)
    c: Coincident(g125,g126)
    c: Coincident(g126,g127)
    c: Coincident(g127,g128)
    c: Coincident(g128,g125)
    c: Horizontal(g125)
    c: Horizontal(g127)
    c: Vertical(g126)
    c: Vertical(g128)
    c: Coincident(g125,g-62)
    c: Coincident(g126,g-63)
    c: Coincident(g129,g130)
    c: Coincident(g130,g131)
    c: Coincident(g131,g132)
    c: Coincident(g132,g129)
    c: Horizontal(g129)
    c: Horizontal(g131)
    c: Vertical(g130)
    c: Vertical(g132)
    c: Coincident(g129,g-60)
    c: Coincident(g130,g-61)
    c: Coincident(g133,g134)
    c: Coincident(g134,g135)
    c: Coincident(g135,g136)
    c: Coincident(g136,g133)
    c: Horizontal(g133)
    c: Horizontal(g135)
    c: Vertical(g134)
    c: Vertical(g136)
    c: Coincident(g133,g-58)
    c: Coincident(g134,g-59)
    c: Coincident(g137,g138)
    c: Coincident(g138,g139)
    c: Coincident(g139,g140)
    c: Coincident(g140,g137)
    c: Horizontal(g137)
    c: Horizontal(g139)
    c: Vertical(g138)
    c: Vertical(g140)
    c: Coincident(g137,g-56)
    c: Coincident(g138,g-57)
    c: Coincident(g141,g142)
    c: Coincident(g142,g143)
    c: Coincident(g143,g144)
    c: Coincident(g144,g141)
    c: Horizontal(g141)
    c: Horizontal(g143)
    c: Vertical(g142)
    c: Vertical(g144)
    c: Coincident(g141,g-74)
    c: Coincident(g142,g-75)
    c: Coincident(g145,g146)
    c: Coincident(g146,g147)
    c: Coincident(g147,g148)
    c: Coincident(g148,g145)
    c: Horizontal(g145)
    c: Horizontal(g147)
    c: Vertical(g146)
    c: Vertical(g148)
    c: Coincident(g145,g-72)
    c: Coincident(g146,g-73)
    c: Coincident(g149,g150)
    c: Coincident(g150,g151)
    c: Coincident(g151,g152)
    c: Coincident(g152,g149)
    c: Horizontal(g149)
    c: Horizontal(g151)
    c: Vertical(g150)
    c: Vertical(g152)
    c: Coincident(g149,g-70)
    c: Coincident(g150,g-71)
    c: Coincident(g-14,g153)
    c: Coincident(g153,g-14)
    c: Coincident(g153,g154)
    c: Coincident(g154,g-15)
    c: Coincident(g154,g155)
    c: Coincident(g155,g-15)
    c: Coincident(g155,g156)
    c: Coincident(g156,g153)
    c: Coincident(g157,g-42)
    c: Coincident(g158,g-43)
    c: Coincident(g159,g-69)
    c: Coincident(g160,g-68)
    c: Coincident(g161,g-76)
    c: Equal(g157,g158)
    c: Equal(g158,g159)
    c: Equal(g159,g160)
    c: Equal(g160,g-76)
    c: Equal(g-76,g161)
    c: PointOnObject(g167,g13)
    c: PointOnObject(g167,g29)
    c: Coincident(g168,g167)
    c: Coincident(g168,g24)
    c: Coincident(g169,g167)
    c: Coincident(g169,g25)
    c: Equal(g168,g169)
    c: Coincident(g170,g6)
    c: Coincident(g170,g167)
    c: Coincident(g171,g5)
    c: Coincident(g171,g167)
    c: Equal(g171,g170)
    c: PointOnObject(g172,g14)
    c: PointOnObject(g172,g30)
    c: Coincident(g173,g172)
    c: Coincident(g173,g30)
    c: Parallel(g173,g172)
    c: Coincident(g174,g23)
    c: Coincident(g174,g172)
    c: Coincident(g175,g172)
    c: Coincident(g175,g22)
    c: Equal(g175,g174)
    c: PointOnObject(g176,g16)
    c: PointOnObject(g176,g31)
    c: Coincident(g177,g21)
    c: Coincident(g177,g176)
    c: Coincident(g178,g176)
    c: Coincident(g178,g20)
    c: Coincident(g179,g7)
    c: Coincident(g179,g176)
    c: Coincident(g180,g176)
    c: Coincident(g180,g2)
    c: Equal(g180,g179)
    c: Equal(g177,g178)
    c: PointOnObject(g181,g12)
    c: PointOnObject(g181,g26)
    c: Coincident(g182,g26)
    c: Coincident(g182,g181)
    c: Coincident(g183,g181)
    c: Coincident(g183,g20)
    c: Coincident(g184,g2)
    c: Coincident(g184,g181)
    c: Coincident(g185,g181)
    c: Coincident(g185,g11)
    c: Equal(g182,g183)
    c: Equal(g184,g185)
    c: Equal(g162,g163)
    c: Equal(g163,g164)
    c: Equal(g164,g165)
    c: Equal(g165,g166)
    c: Diameter(g162) = 3.2
    c: PointOnObject(g162,g181)
    c: PointOnObject(g181,g162)
    c: PointOnObject(g163,g176)
    c: Tangent(g163,g31)
    c: Tangent(g164,g30)
    c: PointOnObject(g164,g172)
    c: Tangent(g165,g29)
    c: PointOnObject(g165,g167)
    c: Coincident(g186,g9)
    c: Coincident(g186,g28)
    c: PointOnObject(g28,g166)
    c: PointOnObject(g166,g186)
FEATURE [PartDesign::Pad] Pad005  label="p_top_plate"
  Direction = (0,0,1)
  Length = 3
  Length2 = 10
  Profile = -> Sketch008
  ReferenceAxis = -> Sketch008 [N_Axis]
  Type = 0
  expr: Length = <<ss_top_plate>>.thickness
FEATURE [PartDesign::CoordinateSystem] mount_hole_b
  AttacherType = Attacher::AttachEngine3D
  MapMode = 11
  Placement = pos=(122.864,27.6957,0) rot=(0,0,1;1.5708rad)
  Support = -> [Sketch008]
FEATURE [PartDesign::Body] Body004  label="top_plate_no_spline"
  Group = -> [ShapeBinder002,Sketch008,Pad005,mount_hole_b]
  Origin = -> Origin010
  Tip = -> Pad005
COMPONENT P3 — recipe-attached ("case_base", modeled in this document).
Construction recipe (the document's own serialized feature program — sketch geometry with constraints, then the solid features built on it; lengths are millimeters unless a unit is written):

FEATURE [PartDesign::Plane] DatumPlane
  AttachmentOffset = pos=(0,0,13.56) rot=(0,0,1;0rad)
  Length = 135.867
  MapMode = 5
  Placement = pos=(-13.56,3e-15,-3e-15) rot=(-0.57735,0.57735,0.57735;4.18879rad)
  ResizeMode = 0
  Support = -> [YZ_Plane003]
  Width = 65.5147
  expr: .AttachmentOffset.Base.z = <<ss_case>>.hole_plane_offset
FEATURE [PartDesign::ShapeBinder] ShapeBinder  label="sb_top_plate"
  Placement = pos=(0,0,3) rot=(0,0,1;0rad)
  Support = -> [Pad005]
  TraceSupport = false
FEATURE [Sketcher::SketchObject] Sketch009
  ExternalGeometry = -> [ShapeBinder]
  FullyConstrained = true
  MapMode = 5
  Support = -> [XY_Plane003]
  expr: Constraints[23] = <<ss_case>>.wall_offset
  sketch-geometry (21):
    g0: LineSegment StartX=2.02396 StartY=64.7101 StartZ=0 EndX=84.3125 EndY=64.7101 EndZ=0
    g1: LineSegment StartX=-13.5556 StartY=49.1305 StartZ=0 EndX=-13.5556 EndY=-1.38632 EndZ=0
    g2: LineSegment StartX=-3.50636 StartY=-36.8919 StartZ=0 EndX=9.94659 EndY=-59.7841 EndZ=0
    g3: LineSegment StartX=27.5142 StartY=-64.4085 StartZ=0 EndX=38.2145 EndY=-58.2148 EndZ=0
    g4: LineSegment StartX=38.2145 StartY=-58.2148 StartZ=0 EndX=93.9034 EndY=-58.2148 EndZ=0
    g5: LineSegment StartX=107.631 StartY=-43.4928 StartZ=0 EndX=141.022 EndY=-43.4928 EndZ=0
    g6: LineSegment StartX=154.772 StartY=-29.7428 StartZ=0 EndX=154.772 EndY=46.1101 EndZ=0
    g7: ArcOfCircle CenterX=139.192 CenterY=46.1101 CenterZ=0 NormalX=0 NormalY=0 NormalZ=1 AngleXU=0 Radius=15.5796 StartAngle=1e-16 EndAngle=1.46083
    g8: ArcOfCircle CenterX=84.3125 CenterY=-450.952 CenterZ=0 NormalX=0 NormalY=0 NormalZ=1 AngleXU=0 Radius=515.662 StartAngle=1.46083 EndAngle=1.5708
    g9: ArcOfCircle CenterX=59.4385 CenterY=0.0985715 CenterZ=0 NormalX=0 NormalY=0 NormalZ=1 AngleXU=0 Radius=73.0092 StartAngle=3.16193 EndAngle=3.67289
    g10: ArcOfCircle CenterX=2.02396 CenterY=49.1305 CenterZ=0 NormalX=0 NormalY=0 NormalZ=1 AngleXU=0 Radius=15.5796 StartAngle=1.5708 EndAngle=3.14159
    g11: ArcOfCircle CenterX=93.9034 CenterY=-44.4872 CenterZ=0 NormalX=0 NormalY=0 NormalZ=1 AngleXU=0 Radius=13.7276 StartAngle=4.71239 EndAngle=6.28319
    g12: ArcOfCircle CenterX=21.0579 CenterY=-53.2544 CenterZ=0 NormalX=0 NormalY=0 NormalZ=1 AngleXU=0 Radius=12.8879 StartAngle=3.67289 EndAngle=5.2371
    g13: ArcOfCircle CenterX=141.022 CenterY=-29.7428 CenterZ=0 NormalX=0 NormalY=0 NormalZ=1 AngleXU=0 Radius=13.75 StartAngle=4.71239 EndAngle=6.28319
    g14: LineSegment StartX=-3.50636 StartY=-36.8919 StartZ=0 EndX=1.01993 EndY=-34.232 EndZ=0
    g15: LineSegment StartX=149.522 StartY=-29.7428 StartZ=0 EndX=154.772 EndY=-29.7428 EndZ=0
    g16: LineSegment StartX=84.3125 StartY=59.4601 StartZ=0 EndX=84.3125 EndY=64.7101 EndZ=0
    g17: LineSegment StartX=141.022 StartY=-43.4928 StartZ=0 EndX=141.022 EndY=-38.2428 EndZ=0
    g18: LineSegment StartX=93.9034 StartY=-52.9648 StartZ=0 EndX=93.9034 EndY=-58.2148 EndZ=0
    g19: LineSegment StartX=27.5142 StartY=-64.4085 StartZ=0 EndX=24.8842 EndY=-59.8648 EndZ=0
    g20: LineSegment StartX=107.631 StartY=-44.4872 StartZ=0 EndX=107.631 EndY=-43.4928 EndZ=0
  constraints (49):
    c: Horizontal(g0)
    c: Vertical(g1)
    c: Coincident(g3,g4)
    c: Horizontal(g4)
    c: Horizontal(g5)
    c: Vertical(g6)
    c: Tangent(g8,g0) = 1.5708
    c: Tangent(g8,g7) = -1.5708
    c: Coincident(g9,g2)
    c: Coincident(g9,g1)
    c: Tangent(g1,g10) = -1.5708
    c: Tangent(g0,g10) = 1.5708
    c: Tangent(g4,g11) = -1.5708
    c: Tangent(g3,g12) = -1.5708
    c: Tangent(g2,g12) = -1.5708
    c: Tangent(g5,g13) = -1.5708
    c: Tangent(g6,g13) = -1.5708
    c: Coincident(g14,g2)
    c: Coincident(g15,g6)
    c: Coincident(g16,g0)
    c: Coincident(g17,g5)
    c: Coincident(g18,g4)
    c: Equal(g18,g17)
    c: DistanceY(g16,g16) = 5.25
    c: Tangent(g7,g6) = -1.5708
    c: Coincident(g19,g3)
    c: Equal(g19,g16)
    c: Equal(g10,g7)
    c: Coincident(g7,g-5)
    c: Coincident(g16,g-4)
    c: Horizontal(g15)
    c: Coincident(g17,g-6)
    c: Vertical(g17)
    c: Coincident(g-4,g8)
    c: Coincident(g15,g-6)
    c: Coincident(g11,g-7)
    c: Coincident(g-7,g18)
    c: Coincident(g19,g-8)
    c: Perpendicular(g3,g19)
    c: Coincident(g12,g-8)
    c: Perpendicular(g2,g14)
    c: Coincident(g14,g-9)
    c: Coincident(g-9,g9)
    c: Parallel(g2,g-10)
    c: Horizontal(g1,g-9)
    c: Coincident(g11,g20)
    c: Coincident(g20,g5)
    c: Vertical(g20)
    c: Horizontal(g11,g-7)
FEATURE [PartDesign::Pad] Pad  label="p_base"
  Direction = (0,0,1)
  Length = 15.4
  Length2 = 10
  Profile = -> Sketch009
  ReferenceAxis = -> Sketch009 [N_Axis]
  Reversed = true
  Type = 0
  expr: Length = <<ss_case>>.base_thickness
FEATURE [Sketcher::SketchObject] Sketch010
  ExternalGeometry = -> [ShapeBinder]
  FullyConstrained = true
  MapMode = 5
  Support = -> [XY_Plane003]
  expr: Constraints[22] = <<ss_case>>.pcb_pocket_offset
  sketch-geometry (24):
    g0: LineSegment StartX=84.3125 StartY=60.4601 StartZ=0 EndX=2.0249 EndY=60.4601 EndZ=0
    g1: LineSegment StartX=-9.30471 StartY=49.1305 StartZ=0 EndX=-9.30471 EndY=-1.38632 EndZ=0
    g2: LineSegment StartX=150.522 StartY=46.1101 StartZ=0 EndX=150.522 EndY=-29.7428 EndZ=0
    g3: LineSegment StartX=141.022 StartY=-39.2428 StartZ=0 EndX=103.381 EndY=-39.2428 EndZ=0
    g4: LineSegment StartX=103.381 StartY=-39.2428 StartZ=0 EndX=103.381 EndY=-44.4872 EndZ=0
    g5: LineSegment StartX=93.9034 StartY=-53.9648 StartZ=0 EndX=37.0732 EndY=-53.9648 EndZ=0
    g6: LineSegment StartX=37.0732 StartY=-53.9648 StartZ=0 EndX=25.3851 EndY=-60.7302 EndZ=0
    g7: LineSegment StartX=13.6107 StartY=-57.6308 StartZ=0 EndX=0.157777 EndY=-34.7386 EndZ=0
    g8: ArcOfCircle CenterX=84.3125 CenterY=-450.952 CenterZ=0 NormalX=0 NormalY=0 NormalZ=1 AngleXU=0 Radius=511.412 StartAngle=1.46083 EndAngle=1.5708
    g9: ArcOfCircle CenterX=139.192 CenterY=46.1101 CenterZ=0 NormalX=0 NormalY=0 NormalZ=1 AngleXU=0 Radius=11.3296 StartAngle=0 EndAngle=1.46083
    g10: ArcOfCircle CenterX=2.0249 CenterY=49.1305 CenterZ=0 NormalX=0 NormalY=0 NormalZ=1 AngleXU=0 Radius=11.3296 StartAngle=1.5708 EndAngle=3.14159
    g11: ArcOfCircle CenterX=21.0579 CenterY=-53.2544 CenterZ=0 NormalX=0 NormalY=0 NormalZ=1 AngleXU=0 Radius=8.63788 StartAngle=3.67289 EndAngle=5.2371
    g12: ArcOfCircle CenterX=93.9034 CenterY=-44.4872 CenterZ=0 NormalX=0 NormalY=0 NormalZ=1 AngleXU=0 Radius=9.47761 StartAngle=4.71239 EndAngle=6.28319
    g13: ArcOfCircle CenterX=141.022 CenterY=-29.7428 CenterZ=0 NormalX=0 NormalY=0 NormalZ=1 AngleXU=0 Radius=9.5 StartAngle=4.71239 EndAngle=6.28319
    g14: LineSegment StartX=25.3851 StartY=-60.7302 StartZ=0 EndX=24.8842 EndY=-59.8648 EndZ=0
    g15: LineSegment StartX=13.6107 StartY=-57.6308 StartZ=0 EndX=14.4729 EndY=-57.1242 EndZ=0
    g16: LineSegment StartX=103.381 StartY=-44.4872 StartZ=0 EndX=102.381 EndY=-44.4872 EndZ=0
    g17: LineSegment StartX=141.022 StartY=-39.2428 StartZ=0 EndX=141.022 EndY=-38.2428 EndZ=0
    g18: LineSegment StartX=150.522 StartY=-29.7428 StartZ=0 EndX=149.522 EndY=-29.7428 EndZ=0
    g19: LineSegment StartX=84.3125 StartY=59.4601 StartZ=0 EndX=84.3125 EndY=60.4601 EndZ=0
    g20: LineSegment StartX=93.9034 StartY=-53.9648 StartZ=0 EndX=93.9034 EndY=-52.9648 EndZ=0
    g21: LineSegment StartX=0.157777 StartY=-34.7386 StartZ=0 EndX=1.01993 EndY=-34.232 EndZ=0
    g22: LineSegment StartX=-9.30471 StartY=-1.38632 StartZ=0 EndX=-8.30447 EndY=-1.38632 EndZ=0
    g23: ArcOfCircle CenterX=59.4385 CenterY=0.0985715 CenterZ=0 NormalX=0 NormalY=0 NormalZ=1 AngleXU=0 Radius=68.7592 StartAngle=3.16319 EndAngle=3.67289
  constraints (55):
    c: Horizontal(g0)
    c: Vertical(g2)
    c: Horizontal(g3)
    c: Coincident(g3,g4)
    c: Vertical(g4)
    c: Horizontal(g5)
    c: Coincident(g5,g6)
    c: Tangent(g2,g9) = 1.5708
    c: Tangent(g8,g9) = -1.5708
    c: Tangent(g8,g0) = -1.5708
    c: Tangent(g1,g10) = -1.5708
    c: Tangent(g0,g10) = -1.5708
    c: Equal(g10,g9)
    c: Tangent(g7,g11) = 1.5708
    c: Tangent(g6,g11) = 1.5708
    c: Tangent(g5,g12) = 1.5708
    c: Tangent(g4,g12) = 1.5708
    c: Tangent(g3,g13) = 1.5708
    c: Tangent(g2,g13) = 1.5708
    c: Coincident(g14,g6)
    c: Coincident(g15,g7)
    c: Horizontal(g16)
    c: Coincident(g17,g3) = 1
    c: Coincident(g18,g2)
    c: Coincident(g19,g0)
    c: Vertical(g1)
    c: DistanceY(g19,g19) = 1
    c: Equal(g16,g14)
    c: Coincident(g19,g-11)
    c: Coincident(g9,g-10)
    c: Coincident(g-9,g13)
    c: Coincident(g18,g-9)
    c: Coincident(g17,g-9)
    c: Coincident(g8,g-11)
    c: Coincident(g16,g-8)
    c: Coincident(g16,g4)
    c: Coincident(g20,g5)
    c: Coincident(g20,g-12)
    c: Vertical(g20)
    c: Equal(g20,g19)
    c: Parallel(g-13,g6)
    c: Perpendicular(g-15,g15)
    c: Coincident(g15,g-15)
    c: Coincident(g14,g-14)
    c: Perpendicular(g6,g14)
    c: Coincident(g21,g7)
    c: Coincident(g21,g-16)
    c: Parallel(g7,g-15)
    c: Perpendicular(g-15,g21)
    c: Coincident(g22,g1)
    c: Coincident(g22,g-17)
    c: Perpendicular(g1,g22)
    c: Coincident(g23,g-16)
    c: Coincident(g23,g7)
    c: Coincident(g23,g1)
FEATURE [PartDesign::Pocket] Pocket  label="c_top_plate_cutout"
  BaseFeature = -> Pad
  Direction = (0,0,-1)
  Length = 4
  Length2 = 5
  Profile = -> Sketch010
  ReferenceAxis = -> Sketch010 [N_Axis]
  Type = 0
  expr: Length = <<ss_case>>.top_plate_cutout_depth
FEATURE [Sketcher::SketchObject] Sketch011
  ExternalGeometry = -> [ShapeBinder]
  FullyConstrained = true
  MapMode = 5
  Support = -> [XY_Plane003]
  sketch-geometry (19):
    g0: LineSegment StartX=-2.30447 StartY=53.4601 StartZ=0 EndX=84.3125 EndY=53.4601 EndZ=0
    g1: LineSegment StartX=6.19146 StartY=-31.1928 StartZ=0 EndX=19.6444 EndY=-54.0851 EndZ=0
    g2: LineSegment StartX=21.8792 StartY=-54.6733 StartZ=0 EndX=35.1965 EndY=-46.9648 EndZ=0
    g3: LineSegment StartX=35.1965 StartY=-46.9648 StartZ=0 EndX=93.9034 EndY=-46.9648 EndZ=0
    g4: LineSegment StartX=96.381 StartY=-44.4872 StartZ=0 EndX=96.381 EndY=-34.7428 EndZ=0
    g5: LineSegment StartX=98.881 StartY=-32.2428 StartZ=0 EndX=141.022 EndY=-32.2428 EndZ=0
    g6: LineSegment StartX=143.522 StartY=-29.7428 StartZ=0 EndX=143.522 EndY=46.1101 EndZ=0
    g7: ArcOfCircle CenterX=59.4385 CenterY=0.0985715 CenterZ=0 NormalX=0 NormalY=0 NormalZ=1 AngleXU=0 Radius=61.7608 StartAngle=3.16564 EndAngle=3.67289
    g8: ArcOfCircle CenterX=84.3125 CenterY=-450.952 CenterZ=0 NormalX=0 NormalY=0 NormalZ=1 AngleXU=0 Radius=504.412 StartAngle=1.46083 EndAngle=1.5708
    g9: ArcOfCircle CenterX=139.192 CenterY=46.1101 CenterZ=0 NormalX=0 NormalY=0 NormalZ=1 AngleXU=0 Radius=4.32961 StartAngle=4e-16 EndAngle=1.46083
    g10: LineSegment StartX=84.3125 StartY=53.4601 StartZ=0 EndX=84.3125 EndY=59.4601 EndZ=0
    g11: ArcOfCircle CenterX=141.022 CenterY=-29.7428 CenterZ=0 NormalX=0 NormalY=0 NormalZ=1 AngleXU=0 Radius=2.5 StartAngle=4.71239 EndAngle=6.28319
    g12: ArcOfCircle CenterX=93.9034 CenterY=-44.4872 CenterZ=0 NormalX=0 NormalY=0 NormalZ=1 AngleXU=0 Radius=2.47761 StartAngle=4.71239 EndAngle=6.28319
    g13: ArcOfCircle CenterX=21.0579 CenterY=-53.2544 CenterZ=0 NormalX=0 NormalY=0 NormalZ=1 AngleXU=0 Radius=1.63946 StartAngle=3.67289 EndAngle=5.2371
    g14: LineSegment StartX=96.381 StartY=-44.4872 StartZ=0 EndX=102.381 EndY=-44.4872 EndZ=0
    g15: ArcOfCircle CenterX=98.881 CenterY=-34.7428 CenterZ=0 NormalX=0 NormalY=0 NormalZ=1 AngleXU=0 Radius=2.5 StartAngle=1.5708 EndAngle=3.14159
    g16: LineSegment StartX=-2.30447 StartY=-1.38632 StartZ=0 EndX=-2.30447 EndY=53.4601 EndZ=0
    g17: LineSegment StartX=-8.30447 StartY=-1.38632 StartZ=0 EndX=-2.30447 EndY=-1.38632 EndZ=0
    g18: LineSegment StartX=1.01993 StartY=-34.232 StartZ=0 EndX=6.19146 EndY=-31.1928 EndZ=0
  constraints (42):
    c: Horizontal(g0)
    c: Coincident(g2,g3)
    c: Horizontal(g3)
    c: Horizontal(g5)
    c: Vertical(g6)
    c: Tangent(g9,g8) = -1.5708
    c: Tangent(g8,g0) = 1.5708
    c: Tangent(g9,g6) = -1.5708
    c: Coincident(g10,g0)
    c: DistanceY(g10,g10) = 6
    c: Tangent(g5,g11) = -1.5708
    c: Tangent(g6,g11) = -1.5708
    c: Tangent(g4,g12) = -1.5708
    c: Tangent(g3,g12) = -1.5708
    c: Vertical(g4)
    c: Tangent(g2,g13) = -1.5708
    c: Tangent(g1,g13) = -1.5708
    c: Coincident(g14,g4)
    c: Equal(g14,g10)
    c: Tangent(g4,g15) = 1.5708
    c: Tangent(g5,g15) = 1.5708
    c: Equal(g15,g11)
    c: Tangent(g7,g1) = -1.5708
    c: Coincident(g16,g7)
    c: Coincident(g16,g0)
    c: Vertical(g16)
    c: Coincident(g17,g7)
    c: Horizontal(g17)
    c: Equal(g10,g17)
    c: Coincident(g8,g-10)
    c: Coincident(g14,g-16)
    c: Coincident(g10,g-10)
    c: Coincident(g11,g-13)
    c: Coincident(g9,g-11)
    c: Coincident(g-16,g12)
    c: Coincident(g-19,g13)
    c: Parallel(g2,g-18)
    c: Parallel(g1,g-3)
    c: Coincident(g17,g-6)
    c: Coincident(g18,g-4)
    c: Coincident(g18,g1)
    c: Coincident(g7,g-4)
FEATURE [Sketcher::SketchObject] Sketch012
  ExternalGeometry = -> [ShapeBinder,Sketch009]
  FullyConstrained = true
  MapMode = 5
  Support = -> [XY_Plane003]
  expr: Constraints[16] = <<ss_case>>.wall_offset - <<ss_case>>.flange_thickness - <<ss_case>>.flange_offset
  sketch-geometry (26):
    g0: LineSegment StartX=-11.3045 StartY=49.1305 StartZ=0 EndX=-11.3045 EndY=-1.38632 EndZ=0
    g1: LineSegment StartX=2.02513 StartY=62.4601 StartZ=0 EndX=84.3125 EndY=62.4601 EndZ=0
    g2: LineSegment StartX=93.9034 StartY=-55.9648 StartZ=0 EndX=37.6103 EndY=-55.9648 EndZ=0
    g3: LineSegment StartX=37.6103 StartY=-55.9648 StartZ=0 EndX=26.3871 EndY=-62.4612 EndZ=0
    g4: LineSegment StartX=11.8874 StartY=-58.6444 StartZ=0 EndX=-1.56593 EndY=-35.7516 EndZ=0
    g5: ArcOfCircle CenterX=141.022 CenterY=-29.7428 CenterZ=0 NormalX=0 NormalY=0 NormalZ=1 AngleXU=0 Radius=11.5 StartAngle=4.71239 EndAngle=6.28319
    g6: ArcOfCircle CenterX=21.0582 CenterY=-53.255 CenterZ=0 NormalX=0 NormalY=0 NormalZ=1 AngleXU=0 Radius=10.6372 StartAngle=3.67289 EndAngle=5.2371
    g7: ArcOfCircle CenterX=2.02513 CenterY=49.1305 CenterZ=0 NormalX=0 NormalY=0 NormalZ=1 AngleXU=0 Radius=13.3296 StartAngle=1.5708 EndAngle=3.14159
    g8: ArcOfCircle CenterX=139.192 CenterY=46.1101 CenterZ=0 NormalX=0 NormalY=0 NormalZ=1 AngleXU=0 Radius=13.3296 StartAngle=0 EndAngle=1.46083
    g9: ArcOfCircle CenterX=84.3125 CenterY=-450.952 CenterZ=0 NormalX=0 NormalY=0 NormalZ=1 AngleXU=0 Radius=513.412 StartAngle=1.46083 EndAngle=1.5708
    g10: ArcOfCircle CenterX=59.4385 CenterY=0.0985715 CenterZ=0 NormalX=0 NormalY=0 NormalZ=1 AngleXU=0 Radius=70.7586 StartAngle=3.16258 EndAngle=3.67289
    g11: LineSegment StartX=84.3125 StartY=59.4601 StartZ=0 EndX=84.3125 EndY=62.4601 EndZ=0
    g12: LineSegment StartX=149.522 StartY=-29.7428 StartZ=0 EndX=152.522 EndY=-29.7428 EndZ=0
    g13: LineSegment StartX=-8.30447 StartY=-1.38632 StartZ=0 EndX=-11.3045 EndY=-1.38632 EndZ=0
    g14: LineSegment StartX=141.022 StartY=-41.2428 StartZ=0 EndX=105.381 EndY=-41.2428 EndZ=0
    g15: LineSegment StartX=93.9034 StartY=-55.9648 StartZ=0 EndX=93.9034 EndY=-52.9648 EndZ=0
    g16: LineSegment StartX=105.381 StartY=-41.2428 StartZ=0 EndX=105.381 EndY=-44.4872 EndZ=0
    g17: ArcOfCircle CenterX=93.9034 CenterY=-44.4872 CenterZ=0 NormalX=0 NormalY=0 NormalZ=1 AngleXU=0 Radius=11.4776 StartAngle=4.71239 EndAngle=6.28319
    g18: LineSegment StartX=152.522 StartY=-29.7428 StartZ=0 EndX=152.522 EndY=46.1101 EndZ=0
    g19: LineSegment StartX=-1.56593 StartY=-35.7516 StartZ=0 EndX=1.01993 EndY=-34.232 EndZ=0
    g20: LineSegment StartX=105.381 StartY=-44.4872 StartZ=0 EndX=102.381 EndY=-44.4872 EndZ=0
    g21: LineSegment StartX=26.3871 StartY=-62.4612 StartZ=0 EndX=24.8842 EndY=-59.8648 EndZ=0
    g22: LineSegment StartX=-13.5556 StartY=64.7101 StartZ=0 EndX=154.772 EndY=64.7101 EndZ=0
    g23: LineSegment StartX=154.772 StartY=64.7101 StartZ=0 EndX=154.772 EndY=-66.1423 EndZ=0
    g24: LineSegment StartX=154.772 StartY=-66.1423 StartZ=0 EndX=-13.5556 EndY=-66.1423 EndZ=0
    g25: LineSegment StartX=-13.5556 StartY=-66.1423 StartZ=0 EndX=-13.5556 EndY=64.7101 EndZ=0
  constraints (64):
    c: Vertical(g0)
    c: Horizontal(g2)
    c: Coincident(g2,g3)
    c: Horizontal(g1)
    c: Coincident(g12,g5) = 1.5708
    c: Tangent(g4,g6) = 1.5708
    c: Tangent(g3,g6) = 1.5708
    c: Tangent(g0,g7) = -1.5708
    c: Tangent(g1,g7) = 1.5708
    c: Tangent(g9,g8) = -1.5708
    c: Tangent(g9,g1) = 1.5708
    c: Equal(g8,g7)
    c: Coincident(g10,g0)
    c: Coincident(g10,g4)
    c: Coincident(g11,g1)
    c: Coincident(g13,g0)
    c: DistanceY(g11,g11) = 3
    c: Horizontal(g14)
    c: Coincident(g15,g2)
    c: Equal(g15,g12)
    c: Coincident(g16,g14)
    c: Coincident(g17,g2)
    c: Tangent(g17,g16) = 1.5708
    c: Vertical(g15)
    c: Coincident(g11,g-15)
    c: Coincident(g12,g-12)
    c: Coincident(g15,g-8)
    c: Coincident(g13,g-3)
    c: Perpendicular(g0,g13)
    c: Equal(g13,g11)
    c: Parallel(g4,g-4)
    c: Parallel(g3,g-6)
    c: Equal(g15,g11)
    c: Coincident(g9,g-25)
    c: Coincident(g8,g-24)
    c: Tangent(g14,g5) = 1.5708
    c: Vertical(g5,g-11)
    c: Horizontal(g16,g-9)
    c: Vertical(g18)
    c: Tangent(g18,g8) = -1.5708
    c: Tangent(g18,g5) = -1.5708
    c: Coincident(g19,g4)
    c: Coincident(g19,g-4)
    c: Perpendicular(g4,g19)
    c: Coincident(g20,g16)
    c: Coincident(g20,g-9)
    c: Coincident(g10,g-3)
    c: Coincident(g21,g3)
    c: Coincident(g21,g-6)
    c: Perpendicular(g-6,g21)
    c: Equal(g21,g15)
    c: Coincident(g17,g-8)
    c: Coincident(g22,g23)
    c: Coincident(g23,g24)
    c: Coincident(g24,g25)
    c: Coincident(g25,g22)
    c: Horizontal(g22)
    c: Horizontal(g24)
    c: Vertical(g23)
    c: Vertical(g25)
    c: Tangent(g24,g-27)
    c: PointOnObject(g-19,g25)
    c: PointOnObject(g-26,g22)
    c: PointOnObject(g-24,g23)
FEATURE [PartDesign::Pocket] Pocket002  label="c_pcb"
  BaseFeature = -> Pocket
  Direction = (0,0,-1)
  Length = 2
  Length2 = 5
  Profile = -> Sketch012
  ReferenceAxis = -> Sketch012 [N_Axis]
  Type = 0
  expr: Length = <<ss_case>>.flange_thickness
FEATURE [PartDesign::Pocket] Pocket001  label="c_flange"
  BaseFeature = -> Pocket002
  Direction = (0,0,-1)
  Length = 12.4
  Length2 = 5
  Profile = -> Sketch011
  ReferenceAxis = -> Sketch011 [N_Axis]
  Type = 0
  expr: Length = <<ss_case>>.base_thickness - <<ss_case>>.wall_thickness
FEATURE [Sketcher::SketchObject] Sketch
  ExternalGeometry = -> [ShapeBinder]
  FullyConstrained = true
  MapMode = 5
  Placement = pos=(0,0,0) rot=(0.57735,0.57735,0.57735;2.0944rad)
  Support = -> [YZ_Plane003]
  expr: Constraints[13] = <<ss_case>>.base_thickness - <<ss_case>>.wall_thickness - <<ss_case>>.connector_z_offset - <<ss_usbc>>.pcb_thickness + <<ss_usbc>>.connector_cutout_offset / 2
  expr: Constraints[6] = <<ss_usbc>>.connector_cutout_width - <<ss_usbc>>.connector_cutout_height
  expr: Constraints[7] = <<ss_usbc>>.connector_cutout_height
  sketch-geometry (7):
    g0: ArcOfCircle CenterX=29.0412 CenterY=-8.52 CenterZ=0 NormalX=0 NormalY=0 NormalZ=1 AngleXU=0 Radius=1.53 StartAngle=1.5708 EndAngle=4.71239
    g1: ArcOfCircle CenterX=34.8212 CenterY=-8.52 CenterZ=0 NormalX=0 NormalY=0 NormalZ=1 AngleXU=0 Radius=1.53 StartAngle=4.71239 EndAngle=7.85398
    g2: LineSegment StartX=29.0412 StartY=-10.05 StartZ=0 EndX=34.8212 EndY=-10.05 EndZ=0
    g3: LineSegment StartX=34.8212 StartY=-6.99 StartZ=0 EndX=29.0412 EndY=-6.99 EndZ=0
    g4: GeomPoint X=31.9312 Y=-8.52 Z=0
    g5: GeomPoint X=31.9312 Y=3 Z=0
    g6: LineSegment StartX=31.9312 StartY=3 StartZ=0 EndX=31.9312 EndY=-10.05 EndZ=0
  constraints (14):
    c: Tangent(g0,g2) = -1.5708
    c: Tangent(g2,g1) = -1.5708
    c: Tangent(g1,g3) = -1.5708
    c: Tangent(g3,g0) = -1.5708
    c: Equal(g0,g1)
    c: Horizontal(g2)
    c: DistanceX(g0,g1) = 5.78
    c: Diameter(g1) = 3.06
    c: Symmetric(g0,g1,g4)
    c: Symmetric(g-3,g-3,g5)
    c: Coincident(g6,g5)
    c: Vertical(g6)
    c: Symmetric(g2,g2,g6)
    c: DistanceY(g6,g-1) = 10.05
FEATURE [PartDesign::Pocket] Pocket003  label="c_usb_c"
  BaseFeature = -> Pocket001
  Direction = (-1,2e-16,-3e-16)
  Length = 5
  Length2 = 5
  Profile = -> Sketch
  ReferenceAxis = -> Sketch [N_Axis]
  Type = 1
FEATURE [Sketcher::SketchObject] Sketch017
  ExternalGeometry = -> [Pocket003,ShapeBinder]
  FullyConstrained = true
  MapMode = 5
  Support = -> [XY_Plane003]
  expr: Constraints[13] = <<ss_case>>.origin_to_inside_flange
  expr: Constraints[8] = <<ss_top_plate>>.gasket_width + 1
  expr: Constraints[9] = <<ss_usbc>>.pcb_width + 1
  sketch-geometry (5):
    g0: LineSegment StartX=-9.3 StartY=43.4312 StartZ=0 EndX=-1.3 EndY=43.4312 EndZ=0
    g1: LineSegment StartX=-1.3 StartY=43.4312 StartZ=0 EndX=-1.3 EndY=20.4312 EndZ=0
    g2: LineSegment StartX=-1.3 StartY=20.4312 StartZ=0 EndX=-9.3 EndY=20.4312 EndZ=0
    g3: LineSegment StartX=-9.3 StartY=20.4312 StartZ=0 EndX=-9.3 EndY=43.4312 EndZ=0
    g4: LineSegment StartX=-1.3 StartY=31.9312 StartZ=0 EndX=27.7393 EndY=31.9312 EndZ=0
  constraints (14):
    c: Coincident(g0,g1)
    c: Coincident(g1,g2)
    c: Coincident(g2,g3)
    c: Coincident(g3,g0)
    c: Horizontal(g0)
    c: Horizontal(g2)
    c: Vertical(g1)
    c: Vertical(g3)
    c: DistanceX(g0,g0) = 8
    c: DistanceY(g1,g1) = 23
    c: Horizontal(g4)
    c: Symmetric(g1,g1,g4)
    c: Symmetric(g-4,g-4,g4)
    c: DistanceX(g2,g-1) = 9.3
FEATURE [PartDesign::Pocket] Pocket004  label="c_usb_c_breakout"
  BaseFeature = -> Pocket003
  Direction = (0,0,-1)
  Length = 11.4
  Length2 = 5
  Profile = -> Sketch017
  ReferenceAxis = -> Sketch017 [N_Axis]
  Type = 0
  expr: Length = <<ss_case>>.base_thickness - <<ss_case>>.wall_thickness - <<ss_case>>.connector_z_offset
FEATURE [Sketcher::SketchObject] Sketch018
  ExternalGeometry = -> [ShapeBinder]
  FullyConstrained = true
  MapMode = 5
  Placement = pos=(-13.56,3e-15,-3e-15) rot=(-0.57735,0.57735,0.57735;4.18879rad)
  Support = -> [DatumPlane]
  expr: .Constraints.usbc_inset_diam = 5 + <<ss_usbc>>.connector_cutout_height
  expr: Constraints[8] = 5 + <<ss_usbc>>.connector_cutout_width - (<<ss_usbc>>.pcb_thickness * 2 + <<ss_usbc>>.connector_cutout_height)
  expr: Constraints[9] = <<ss_case>>.base_thickness - <<ss_case>>.wall_thickness - <<ss_case>>.connector_z_offset - <<ss_usbc>>.pcb_thickness - <<ss_usbc>>.connector_cutout_height / 2
  sketch-geometry (6):
    g0: ArcOfCircle CenterX=-28.1412 CenterY=-8.27 CenterZ=0 NormalX=0 NormalY=0 NormalZ=1 AngleXU=0 Radius=4.03 StartAngle=4.71239 EndAngle=7.85398
    g1: ArcOfCircle CenterX=-35.7212 CenterY=-8.27 CenterZ=0 NormalX=0 NormalY=0 NormalZ=1 AngleXU=0 Radius=4.03 StartAngle=1.5708 EndAngle=4.71239
    g2: LineSegment StartX=-28.1412 StartY=-4.24 StartZ=0 EndX=-35.7212 EndY=-4.24 EndZ=0
    g3: LineSegment StartX=-35.7212 StartY=-12.3 StartZ=0 EndX=-28.1412 EndY=-12.3 EndZ=0
    g4: GeomPoint X=-31.9312 Y=-8.27 Z=0
    g5: LineSegment StartX=-31.9312 StartY=-8.27 StartZ=0 EndX=-31.9312 EndY=3 EndZ=0
  constraints (13):
    c: Tangent(g0,g2) = -1.5708
    c: Tangent(g2,g1) = -1.5708
    c: Tangent(g1,g3) = -1.5708
    c: Tangent(g3,g0) = -1.5708
    c: Equal(g0,g1)
    c: Horizontal(g2)
    c: Symmetric(g0,g1,g4)
    c: Diameter(g0) = 8.06  'usbc_inset_diam'
    c: DistanceX(g2,g2) = 7.58
    c: DistanceY(g0,g-1) = 8.27
    c: Coincident(g5,g4)
    c: Vertical(g5)
    c: Symmetric(g-3,g-3,g5)
FEATURE [Sketcher::SketchObject] Sketch019
  ExternalGeometry = -> [Pocket004,ShapeBinder]
  FullyConstrained = true
  MapMode = 5
  Support = -> [XY_Plane003]
  expr: Constraints[1] = <<ss_usbc>>.hole_spacing
  expr: Constraints[2] = <<ss_case>>.usb_c_screw_hole_od
  expr: Constraints[8] = <<ss_case>>.origin_to_inside_flange - <<ss_usbc>>.hole_inset
  sketch-geometry (4):
    g0: Circle CenterX=-6.7 CenterY=40.2312 CenterZ=0 NormalX=0 NormalY=0 NormalZ=1 AngleXU=0 Radius=1
    g1: Circle CenterX=-6.7 CenterY=23.6312 CenterZ=0 NormalX=0 NormalY=0 NormalZ=1 AngleXU=0 Radius=1
    g2: GeomPoint X=-6.7 Y=31.9312 Z=0
    g3: LineSegment StartX=-6.7 StartY=31.9312 StartZ=0 EndX=27.7393 EndY=31.9312 EndZ=0
  constraints (9):
    c: Equal(g1,g0)
    c: DistanceY(g1,g0) = 16.6
    c: Diameter(g0) = 2
    c: Vertical(g1,g0)
    c: Symmetric(g1,g0,g2)
    c: Coincident(g3,g2)
    c: Horizontal(g3)
    c: Symmetric(g-4,g-4,g3)
    c: DistanceX(g1,g-1) = 6.7
FEATURE [PartDesign::Pocket] Pocket006
  BaseFeature = -> Pocket004
  Direction = (0,0,-1)
  Length = 14.4
  Length2 = 5
  Profile = -> Sketch019
  ReferenceAxis = -> Sketch019 [N_Axis]
  Type = 0
  expr: Length = <<ss_case>>.base_thickness - 1
FEATURE [PartDesign::Pocket] Pocket005
  BaseFeature = -> Pocket006
  Direction = (1,-4e-16,2e-16)
  Length = 3.25
  Length2 = 5
  Profile = -> Sketch018
  ReferenceAxis = -> Sketch018 [N_Axis]
  Type = 0
  expr: Length = <<ss_case>>.wall_thickness + <<ss_case>>.flange_thickness - <<ss_case>>.flange_offset - <<ss_usbc>>.connector_offset
FEATURE [PartDesign::Plane] DatumPlane002
  AttachmentOffset = pos=(0,0,15.4) rot=(0,0,1;0rad)
  Length = 203.507
  MapMode = 5
  Placement = pos=(0,0,-15.4) rot=(0,1,0;3.14159rad)
  ResizeMode = 0
  Support = -> [XY_Plane003]
  Width = 149.338
  expr: .AttachmentOffset.Base.z = <<ss_case>>.base_thickness
FEATURE [Sketcher::SketchObject] Sketch020
  ExternalGeometry = -> [ShapeBinder]
  FullyConstrained = true
  MapMode = 5
  Placement = pos=(0,0,-15.4) rot=(0,1,0;3.14159rad)
  Support = -> [DatumPlane002]
  expr: Constraints[10] = 3
  sketch-geometry (12):
    g0: Circle CenterX=-145.695 CenterY=51.9344 CenterZ=0 NormalX=0 NormalY=0 NormalZ=1 AngleXU=0 Radius=1.5
    g1: Circle CenterX=-145.901 CenterY=-34.6219 CenterZ=0 NormalX=0 NormalY=0 NormalZ=1 AngleXU=0 Radius=1.5
    g2: Circle CenterX=-98.7666 CenterY=-49.3504 CenterZ=0 NormalX=0 NormalY=0 NormalZ=1 AngleXU=0 Radius=1.5
    g3: Circle CenterX=-19.5209 CenterY=-59.0934 CenterZ=0 NormalX=0 NormalY=0 NormalZ=1 AngleXU=0 Radius=1.5
    g4: Circle CenterX=6.70447 CenterY=-1.38632 CenterZ=0 NormalX=0 NormalY=0 NormalZ=1 AngleXU=0 Radius=1.5
    g5: Circle CenterX=4.21834 CenterY=55.374 CenterZ=0 NormalX=0 NormalY=0 NormalZ=1 AngleXU=0 Radius=1.5
    g6: LineSegment StartX=8.30447 StartY=-1.38632 StartZ=0 EndX=8.30447 EndY=49.1305 EndZ=0
    g7: LineSegment StartX=-2.02513 StartY=59.4601 StartZ=0 EndX=-27.7344 EndY=59.4601 EndZ=0
    g8: ArcOfCircle CenterX=-2.02513 CenterY=49.1305 CenterZ=0 NormalX=0 NormalY=0 NormalZ=1 AngleXU=0 Radius=10.3296 StartAngle=0 EndAngle=1.5708
    g9: LineSegment StartX=-2.02513 StartY=49.1305 StartZ=0 EndX=5.279 EndY=56.4346 EndZ=0
    g10: LineSegment StartX=8.30447 StartY=49.1305 StartZ=0 EndX=5.279 EndY=56.4346 EndZ=0
    g11: LineSegment StartX=5.279 StartY=56.4346 StartZ=0 EndX=-2.02513 EndY=59.4601 EndZ=0
  constraints (27):
    c: Coincident(g0,g-7)
    c: Coincident(g1,g-6)
    c: Coincident(g2,g-5)
    c: Coincident(g3,g-3)
    c: Coincident(g4,g-4)
    c: Equal(g0,g1)
    c: Equal(g1,g2)
    c: Equal(g2,g3)
    c: Equal(g3,g4)
    c: Equal(g4,g5)
    c: Diameter(g0) = 3
    c: Coincident(g6,g-9)
    c: Coincident(g7,g-8)
    c: Horizontal(g7)
    c: Tangent(g6,g8) = -1.5708
    c: Tangent(g7,g8) = -1.5708
    c: Vertical(g6)
    c: Equal(g-10,g8)
    c: Tangent(g5,g8)
    c: Coincident(g9,g8)
    c: PointOnObject(g9,g8)
    c: Coincident(g10,g6)
    c: Coincident(g10,g9)
    c: Coincident(g11,g9)
    c: Coincident(g11,g7)
    c: Equal(g10,g11)
    c: PointOnObject(g5,g9)
FEATURE [Sketcher::SketchObject] Sketch021
  ExternalGeometry = -> [Sketch020,ShapeBinder]
  FullyConstrained = true
  MapMode = 5
  Placement = pos=(0,0,-15.4) rot=(0,1,0;3.14159rad)
  Support = -> [DatumPlane002]
  expr: Constraints[10] = 6.8
  sketch-geometry (6):
    g0: Circle CenterX=-145.695 CenterY=51.9344 CenterZ=0 NormalX=0 NormalY=0 NormalZ=1 AngleXU=0 Radius=3.4
    g1: Circle CenterX=-145.901 CenterY=-34.6219 CenterZ=0 NormalX=0 NormalY=0 NormalZ=1 AngleXU=0 Radius=3.4
    g2: Circle CenterX=-98.7666 CenterY=-49.3504 CenterZ=0 NormalX=0 NormalY=0 NormalZ=1 AngleXU=0 Radius=3.4
    g3: Circle CenterX=-19.5209 CenterY=-59.0934 CenterZ=0 NormalX=0 NormalY=0 NormalZ=1 AngleXU=0 Radius=3.4
    g4: Circle CenterX=6.70447 CenterY=-1.38632 CenterZ=0 NormalX=0 NormalY=0 NormalZ=1 AngleXU=0 Radius=3.4
    g5: Circle CenterX=4.21834 CenterY=55.374 CenterZ=0 NormalX=0 NormalY=0 NormalZ=1 AngleXU=0 Radius=3.4
  constraints (12):
    c: Coincident(g0,g-3)
    c: Coincident(g1,g-4)
    c: Coincident(g2,g-5)
    c: Coincident(g3,g-6)
    c: Coincident(g4,g-7)
    c: Equal(g0,g5)
    c: Equal(g5,g4)
    c: Equal(g4,g3)
    c: Equal(g3,g2)
    c: Equal(g2,g1)
    c: Diameter(g5) = 6.8
    c: Coincident(g-9,g5)
FEATURE [PartDesign::Pad] Pad008
  BaseFeature = -> Pocket005
  Direction = (0,0,-1)
  Length = 11.4
  Length2 = 10
  Profile = -> Sketch021
  ReferenceAxis = -> Sketch021 [N_Axis]
  Reversed = true
  Type = 0
  expr: Length = <<ss_case>>.base_thickness - <<ss_case>>.top_plate_cutout_depth
FEATURE [PartDesign::Hole] Hole
  BaseFeature = -> Pad008
  CustomThreadClearance = 0
  Depth = 431.796
  DepthType = 1
  Diameter = 3.2
  DrillForDepth = false
  DrillPoint = 1
  DrillPointAngle = 118
  HoleCutCountersinkAngle = 90
  HoleCutCustomValues = false
  HoleCutDepth = 3.5
  HoleCutDiameter = 6
  HoleCutType = 1
  ModelThread = false
  Profile = -> Sketch020
  Tapered = false
  TaperedAngle = 90
  ThreadClass = 0
  ThreadDepth = 431.796
  ThreadDepthType = 0
  ThreadDirection = 0
  ThreadFit = 0
  ThreadSize = 0
  ThreadType = 0
  Threaded = false
  UseCustomThreadClearance = false
  expr: Diameter = <<ss_case>>.screw_hole_od
  expr: HoleCutDepth = <<ss_case>>.screw_head_height + 0.5
  expr: HoleCutDiameter = <<ss_case>>.screw_head_od + 0.5
FEATURE [Sketcher::SketchObject] Sketch028
  FullyConstrained = true
  MapMode = 5
  Placement = pos=(0,0,0) rot=(1,0,0;1.5708rad)
  Support = -> [XZ_Plane003]
  expr: Constraints[12] = <<ss_case>>.controller_z_offset_max
  expr: Constraints[16] = <<ss_lily58_pcb>>.board_edge_to_controller_centre_max
  sketch-geometry (7):
    g0: LineSegment StartX=9.255 StartY=0 StartZ=0 EndX=24.255 EndY=0 EndZ=0
    g1: LineSegment StartX=24.255 StartY=0 StartZ=0 EndX=24.255 EndY=-5.8 EndZ=0
    g2: LineSegment StartX=23.255 StartY=-6.8 StartZ=0 EndX=10.255 EndY=-6.8 EndZ=0
    g3: LineSegment StartX=9.255 StartY=-5.8 StartZ=0 EndX=9.255 EndY=0 EndZ=0
    g4: ArcOfCircle CenterX=10.255 CenterY=-5.8 CenterZ=0 NormalX=0 NormalY=0 NormalZ=1 AngleXU=0 Radius=1 StartAngle=3.14159 EndAngle=4.71239
    g5: ArcOfCircle CenterX=23.255 CenterY=-5.8 CenterZ=0 NormalX=0 NormalY=0 NormalZ=1 AngleXU=0 Radius=1 StartAngle=4.71239 EndAngle=6.28319
    g6: GeomPoint X=16.755 Y=0 Z=0
  constraints (17):
    c: Coincident(g0,g1)
    c: Coincident(g3,g0)
    c: Horizontal(g0)
    c: Horizontal(g2)
    c: Vertical(g1)
    c: Vertical(g3)
    c: PointOnObject(g0,g-1)
    c: Tangent(g2,g4) = 1.5708
    c: Tangent(g3,g4) = 1.5708
    c: Tangent(g2,g5) = 1.5708
    c: Tangent(g1,g5) = 1.5708
    c: Equal(g5,g4)
    c: DistanceY(g2,g-1) = 6.8
    c: DistanceX(g0,g0) = 15
    c: Diameter(g5) = 2
    c: Symmetric(g0,g0,g6)
    c: DistanceX(g-1,g6) = 16.755
FEATURE [PartDesign::Pocket] Pocket007
  BaseFeature = -> Hole
  Direction = (0,1,2e-16)
  Length = 5
  Length2 = 5
  Profile = -> Sketch028
  ReferenceAxis = -> Sketch028 [N_Axis]
  Type = 1
FEATURE [PartDesign::Fillet] Fillet001
  Base = -> Pocket007 [Face9]
  BaseFeature = -> Pocket007
  Radius = 2.5
  SupportTransform = false
  UseAllEdges = false
FEATURE [PartDesign::Body] Body001  label="case_bottom"
  Group = -> [ShapeBinder,Sketch009,Pad,Sketch010,Pocket,Sketch011,Sketch012,Pocket002,Pocket001,Sketch,Pocket003,Sketch017,Pocket004,DatumPlane,Sketch018,Sketch019,Pocket006,Pocket005,DatumPlane002,Pad008,Sketch020,Hole,Sketch021,Sketch028,Pocket007,Fillet001]
  Origin = -> Origin003
  Tip = -> Fillet001
COMPONENT P4 — recipe-attached ("usbc_breakout", modeled in this document).
Construction recipe (the document's own serialized feature program — sketch geometry with constraints, then the solid features built on it; lengths are millimeters unless a unit is written):

FEATURE [Sketcher::SketchObject] Sketch015
  FullyConstrained = true
  MapMode = 5
  Support = -> [XY_Plane012]
  expr: Constraints[16] = <<ss_usbc>>.hole_spacing
  expr: Constraints[17] = <<ss_usbc>>.hole_inset
  expr: Constraints[18] = <<ss_usbc>>.hole_diameter
  expr: Constraints[21] = <<ss_usbc>>.connector_offset
  expr: Constraints[8] = <<ss_usbc>>.pcb_length
  expr: Constraints[9] = <<ss_usbc>>.pcb_width
  sketch-geometry (9):
    g0: LineSegment StartX=-11 StartY=1.5 StartZ=0 EndX=11 EndY=1.5 EndZ=0
    g1: LineSegment StartX=11 StartY=1.5 StartZ=0 EndX=11 EndY=14.2 EndZ=0
    g2: LineSegment StartX=11 StartY=14.2 StartZ=0 EndX=-11 EndY=14.2 EndZ=0
    g3: LineSegment StartX=-11 StartY=14.2 StartZ=0 EndX=-11 EndY=1.5 EndZ=0
    g4: Circle CenterX=8.3 CenterY=4.1 CenterZ=0 NormalX=0 NormalY=0 NormalZ=1 AngleXU=0 Radius=1.6
    g5: Circle CenterX=-8.3 CenterY=4.1 CenterZ=0 NormalX=0 NormalY=0 NormalZ=1 AngleXU=0 Radius=1.6
    g6: LineSegment StartX=8.3 StartY=4.1 StartZ=0 EndX=-8.3 EndY=4.1 EndZ=0
    g7: GeomPoint X=0 Y=4.1 Z=0
    g8: GeomPoint X=0 Y=1.5 Z=0
  constraints (22):
    c: Coincident(g0,g1)
    c: Coincident(g1,g2)
    c: Coincident(g2,g3)
    c: Coincident(g3,g0)
    c: Horizontal(g0)
    c: Horizontal(g2)
    c: Vertical(g1)
    c: Vertical(g3)
    c: DistanceY(g1,g1) = 12.7
    c: DistanceX(g2,g2) = 22
    c: Equal(g5,g4)
    c: Coincident(g6,g4)
    c: Coincident(g6,g5)
    c: Horizontal(g6)
    c: Symmetric(g6,g6,g7)
    c: Vertical(g7,g-1)
    c: DistanceX(g6,g6) = 16.6
    c: DistanceY(g0,g4) = 2.6
    c: Diameter(g4) = 3.2
    c: Symmetric(g0,g0,g8)
    c: Vertical(g8,g-1)
    c: DistanceY(g-1,g0) = 1.5
FEATURE [PartDesign::Pad] Pad006
  Direction = (0,0,1)
  Length = 1.6
  Length2 = 10
  Profile = -> Sketch015
  ReferenceAxis = -> Sketch015 [N_Axis]
  Reversed = true
  Type = 0
  expr: Length = <<ss_usbc>>.pcb_thickness
FEATURE [Sketcher::SketchObject] Sketch016
  FullyConstrained = true
  MapMode = 5
  Placement = pos=(0,0,0) rot=(1,0,0;1.5708rad)
  Support = -> [XZ_Plane012]
  expr: Constraints[7] = <<ss_usbc>>.connector_height
  expr: Constraints[8] = <<ss_usbc>>.connector_width - <<ss_usbc>>.connector_height
  sketch-geometry (4):
    g0: ArcOfCircle CenterX=-2.89 CenterY=1.28 CenterZ=0 NormalX=0 NormalY=0 NormalZ=1 AngleXU=0 Radius=1.28 StartAngle=1.5708 EndAngle=4.71239
    g1: ArcOfCircle CenterX=2.89 CenterY=1.28 CenterZ=0 NormalX=0 NormalY=0 NormalZ=1 AngleXU=0 Radius=1.28 StartAngle=4.71239 EndAngle=7.85398
    g2: LineSegment StartX=-2.89 StartY=2.0424e-12 StartZ=0 EndX=2.89 EndY=2.0424e-12 EndZ=0
    g3: LineSegment StartX=2.89 StartY=2.56 StartZ=0 EndX=-2.89 EndY=2.56 EndZ=0
  constraints (9):
    c: Tangent(g0,g2) = -1.5708
    c: Tangent(g2,g1) = -1.5708
    c: Tangent(g1,g3) = -1.5708
    c: Tangent(g3,g0) = -1.5708
    c: Equal(g0,g1)
    c: Horizontal(g2)
    c: Symmetric(g2,g2,g-1)
    c: Diameter(g1) = 2.56
    c: DistanceX(g0,g1) = 5.78
FEATURE [PartDesign::Pad] Pad007
  BaseFeature = -> Pad006
  Direction = (0,-1,-2e-16)
  Length = 7.3
  Length2 = 5
  Profile = -> Sketch016
  ReferenceAxis = -> Sketch016 [N_Axis]
  Reversed = true
  Type = 0
  expr: Length = <<ss_usbc>>.connector_depth
  expr: Length2 = 5
FEATURE [PartDesign::Body] Body  label="b_connector"
  Group = -> [Sketch015,Pad006,Sketch016,Pad007]
  Origin = -> Origin012
  Tip = -> Pad007
COMPONENT P5 — recipe-attached ("p_spacer", modeled in this document).
Construction recipe (the document's own serialized feature program — sketch geometry with constraints, then the solid features built on it; lengths are millimeters unless a unit is written):

FEATURE [Sketcher::SketchObject] Sketch022
  FullyConstrained = true
  MapMode = 5
  Support = -> [XY_Plane014]
  expr: Constraints[2] = <<ss_case>>.screw_hole_od
  expr: Constraints[3] = <<ss_case>>.screw_hole_od + 2
  sketch-geometry (2):
    g0: Circle CenterX=0 CenterY=0 CenterZ=0 NormalX=0 NormalY=0 NormalZ=1 AngleXU=0 Radius=1.6
    g1: Circle CenterX=0 CenterY=0 CenterZ=0 NormalX=0 NormalY=0 NormalZ=1 AngleXU=0 Radius=2.6
  constraints (4):
    c: Coincident(g0,g-1)
    c: Coincident(g1,g0)
    c: Diameter(g0) = 3.2
    c: Diameter(g1) = 5.2
FEATURE [PartDesign::Pad] Pad009
  Direction = (0,0,1)
  Length = 3.8
  Length2 = 10
  Profile = -> Sketch022
  ReferenceAxis = -> Sketch022 [N_Axis]
  Type = 0
  expr: Length = <<ss_case>>.top_plate_offset
FEATURE [Sketcher::SketchObject] Sketch023
  FullyConstrained = true
  MapMode = 5
  Support = -> [XY_Plane016]
FEATURE [PartDesign::Body] Body005  label="b_spacer"
  Group = -> [Sketch022,Pad009,Sketch023]
  Origin = -> Origin014
  Tip = -> Pad009
COMPONENT P6 — recipe-attached ("bastard_splinky", modeled in this document).
Construction recipe (the document's own serialized feature program — sketch geometry with constraints, then the solid features built on it; lengths are millimeters unless a unit is written):

FEATURE [PartDesign::ShapeBinder] ShapeBinder003
  Placement = pos=(-147.85,76.2,0) rot=(0,0,1;0rad)
  Support = -> [Board_outline001]
  TraceSupport = false
FEATURE [Sketcher::SketchObject] Sketch024
  ExternalGeometry = -> [ShapeBinder003]
  FullyConstrained = true
  MapMode = 5
  Placement = pos=(0,0,0) rot=(1,0,0;1.5708rad)
  Support = -> [XZ_Plane017]
  expr: Constraints[11] = <<ss_usbc>>.connector_height
  expr: Constraints[12] = <<ss_usbc>>.connector_width
  sketch-geometry (7):
    g0: ArcOfCircle CenterX=1.66 CenterY=1.28 CenterZ=0 NormalX=0 NormalY=0 NormalZ=1 AngleXU=0 Radius=1.28 StartAngle=1.5708 EndAngle=4.71239
    g1: ArcOfCircle CenterX=7.44 CenterY=1.28 CenterZ=0 NormalX=0 NormalY=0 NormalZ=1 AngleXU=0 Radius=1.28 StartAngle=4.71239 EndAngle=7.85398
    g2: LineSegment StartX=1.66 StartY=0 StartZ=0 EndX=7.44 EndY=0 EndZ=0
    g3: LineSegment StartX=7.44 StartY=2.56 StartZ=0 EndX=1.66 EndY=2.56 EndZ=0
    g4: LineSegment StartX=8.72 StartY=1.28 StartZ=0 EndX=0.38 EndY=1.28 EndZ=0
    g5: LineSegment StartX=1.66 StartY=0 StartZ=0 EndX=0 EndY=0 EndZ=0
    g6: LineSegment StartX=7.44 StartY=0 StartZ=0 EndX=9.1 EndY=0 EndZ=0
  constraints (18):
    c: Tangent(g0,g2) = -1.5708
    c: Tangent(g2,g1) = -1.5708
    c: Tangent(g1,g3) = -1.5708
    c: Tangent(g3,g0) = -1.5708
    c: Equal(g0,g1)
    c: Horizontal(g2)
    c: PointOnObject(g1,g-1)
    c: PointOnObject(g4,g1)
    c: PointOnObject(g4,g0)
    c: Horizontal(g4)
    c: PointOnObject(g1,g4)
    c: Diameter(g1) = 2.56
    c: DistanceX(g4,g4) = 8.34
    c: Coincident(g5,g0)
    c: Coincident(g5,g-1)
    c: Coincident(g6,g1)
    c: Coincident(g6,g-3)
    c: Equal(g5,g6)
FEATURE [PartDesign::Pad] Pad010
  Direction = (0,-1,2e-16)
  Length = 5.8
  Length2 = 1.5
  Placement = pos=(0,0,0) rot=(1,0,0;1.5708rad)
  Profile = -> Sketch024
  ReferenceAxis = -> Sketch024 [N_Axis]
  Type = 4
  expr: Length = <<ss_usbc>>.connector_depth - 1.5
FEATURE [PartDesign::Body] Body006  label="Body"
  Group = -> [ShapeBinder003,Sketch024,Pad010]
  Origin = -> Origin017
  Tip = -> Pad010
COMPONENT P7 — recipe-attached ("header_12", modeled in this document).
Construction recipe (the document's own serialized feature program — sketch geometry with constraints, then the solid features built on it; lengths are millimeters unless a unit is written):

FEATURE [Sketcher::SketchObject] Sketch025
  FullyConstrained = true
  MapMode = 5
  Support = -> [XY_Plane018]
  sketch-geometry (1):
    g0: Circle CenterX=0 CenterY=0 CenterZ=0 NormalX=0 NormalY=0 NormalZ=1 AngleXU=0 Radius=0.325
  constraints (2):
    c: Coincident(g0,g-1)
    c: Diameter(g0) = 0.65
FEATURE [PartDesign::Pad] Pad011  label="p_pin"
  Direction = (0,0,1)
  Length = 3
  Length2 = 8.5
  Profile = -> Sketch025
  ReferenceAxis = -> Sketch025 [N_Axis]
  Type = 4
  expr: Length2 = 6 + 2.5
FEATURE [Sketcher::SketchObject] Sketch026
  FullyConstrained = true
  MapMode = 5
  Support = -> [XY_Plane019]
  expr: Constraints[19] = <<ss_header>>.pitch
  expr: Constraints[20] = <<ss_header>>.pitch
  sketch-geometry (12):
    g0: ArcOfCircle CenterX=-0.77 CenterY=-0.77 CenterZ=0 NormalX=0 NormalY=0 NormalZ=1 AngleXU=0 Radius=0.5 StartAngle=3.14159 EndAngle=4.71239
    g1: LineSegment StartX=-1.27 StartY=-0.77 StartZ=0 EndX=-1.27 EndY=0.77 EndZ=0
    g2: ArcOfCircle CenterX=-0.77 CenterY=0.77 CenterZ=0 NormalX=0 NormalY=0 NormalZ=1 AngleXU=0 Radius=0.5 StartAngle=1.5708 EndAngle=3.14159
    g3: LineSegment StartX=-0.77 StartY=1.27 StartZ=0 EndX=0.77 EndY=1.27 EndZ=0
    g4: ArcOfCircle CenterX=0.77 CenterY=0.77 CenterZ=0 NormalX=0 NormalY=0 NormalZ=1 AngleXU=0 Radius=0.5 StartAngle=-1.8e-15 EndAngle=1.5708
    g5: LineSegment StartX=1.27 StartY=0.77 StartZ=0 EndX=1.27 EndY=-0.77 EndZ=0
    g6: ArcOfCircle CenterX=0.77 CenterY=-0.77 CenterZ=0 NormalX=0 NormalY=0 NormalZ=1 AngleXU=0 Radius=0.5 StartAngle=4.71239 EndAngle=6.28319
    g7: LineSegment StartX=0.77 StartY=-1.27 StartZ=0 EndX=-0.77 EndY=-1.27 EndZ=0
    g8: GeomPoint X=-1.27 Y=-1.27 Z=0
    g9: GeomPoint X=1.27 Y=1.27 Z=0
    g10: GeomPoint X=-1.27 Y=0 Z=0
    g11: GeomPoint X=0 Y=1.27 Z=0
  constraints (26):
    c: Tangent(g0,g1) = 1.5708
    c: Tangent(g1,g2) = 1.5708
    c: Tangent(g2,g3) = 1.5708
    c: Tangent(g3,g4) = 1.5708
    c: Tangent(g4,g5) = 1.5708
    c: Tangent(g5,g6) = 1.5708
    c: Tangent(g6,g7) = 1.5708
    c: Tangent(g7,g0) = 1.5708
    c: Horizontal(g3)
    c: Horizontal(g7)
    c: Vertical(g1)
    c: Vertical(g5)
    c: Equal(g0,g2)
    c: Equal(g2,g4)
    c: Equal(g4,g6)
    c: PointOnObject(g8,g1)
    c: PointOnObject(g8,g7)
    c: PointOnObject(g9,g3)
    c: PointOnObject(g9,g5)
    c: DistanceY(g6,g3) = 2.54
    c: DistanceX(g1,g4) = 2.54
    c: Symmetric(g1,g1,g10)
    c: Symmetric(g3,g3,g11)
    c: PointOnObject(g11,g-2)
    c: PointOnObject(g10,g-1)
    c: Diameter(g4) = 1
FEATURE [PartDesign::Pad] Pad012  label="p_spacer003"
  BaseFeature = -> Pad011
  Direction = (0,0,1)
  Length = 2.5
  Length2 = 10
  Profile = -> Sketch026
  ReferenceAxis = -> Sketch026 [N_Axis]
  Reversed = true
  Type = 0
  expr: Length = <<ss_header>>.spacer_height
FEATURE [PartDesign::LinearPattern] LinearPattern
  Direction = -> Sketch026 [H_Axis]
  Length = 27.94
  Occurrences = 12
  expr: Length = <<ss_header>>.pitch * 11
FEATURE [PartDesign::MultiTransform] MultiTransform
  BaseFeature = -> Pad012
  Originals = -> [Pad012,Pad011]
  Transformations = -> [LinearPattern]
FEATURE [Sketcher::SketchObject] Sketch027
  FullyConstrained = true
  MapMode = 5
  Placement = pos=(0,0,0) rot=(1,0,0;1.5708rad)
  Support = -> [XZ_Plane003]
FEATURE [PartDesign::Body] Body007  label="b_header"
  Group = -> [Sketch025,Pad011,Sketch026,Pad012,MultiTransform,LinearPattern,Sketch027]
  Origin = -> Origin019
  Tip = -> MultiTransform
COMPONENT P8 — recipe-attached ("case_cover", modeled in this document).
Construction recipe (the document's own serialized feature program — sketch geometry with constraints, then the solid features built on it; lengths are millimeters unless a unit is written):

FEATURE [PartDesign::ShapeBinder] ShapeBinder004
  Support = -> [Pad005]
  TraceSupport = false
FEATURE [Sketcher::SketchObject] Sketch029
  ExternalGeometry = -> [ShapeBinder004]
  FullyConstrained = true
  MapMode = 5
  Support = -> [XY_Plane021]
  expr: Constraints[40] = <<ss_case>>.wall_offset
  expr: Constraints[65] = <<ss_top_plate>>.gasket_width - 2
  sketch-geometry (41):
    g0: LineSegment StartX=2.02396 StartY=64.7101 StartZ=0 EndX=84.3125 EndY=64.7101 EndZ=0
    g1: LineSegment StartX=154.772 StartY=46.1101 StartZ=0 EndX=154.772 EndY=-29.7428 EndZ=0
    g2: LineSegment StartX=141.022 StartY=-43.4928 StartZ=0 EndX=107.631 EndY=-43.4928 EndZ=0
    g3: LineSegment StartX=93.9034 StartY=-58.2148 StartZ=0 EndX=38.2145 EndY=-58.2148 EndZ=0
    g4: LineSegment StartX=38.2145 StartY=-58.2148 StartZ=0 EndX=27.5142 EndY=-64.4085 EndZ=0
    g5: LineSegment StartX=9.94659 StartY=-59.7841 StartZ=0 EndX=-3.50636 EndY=-36.8919 EndZ=0
    g6: ArcOfCircle CenterX=59.4385 CenterY=0.0985715 CenterZ=0 NormalX=0 NormalY=0 NormalZ=1 AngleXU=0 Radius=73.0092 StartAngle=3.16193 EndAngle=3.67289
    g7: ArcOfCircle CenterX=84.3125 CenterY=-450.952 CenterZ=0 NormalX=0 NormalY=0 NormalZ=1 AngleXU=0 Radius=515.662 StartAngle=1.46083 EndAngle=1.5708
    g8: ArcOfCircle CenterX=139.192 CenterY=46.1101 CenterZ=0 NormalX=0 NormalY=0 NormalZ=1 AngleXU=0 Radius=15.5796 StartAngle=2e-16 EndAngle=1.46083
    g9: ArcOfCircle CenterX=2.02396 CenterY=49.1305 CenterZ=0 NormalX=0 NormalY=0 NormalZ=1 AngleXU=0 Radius=15.5796 StartAngle=1.5708 EndAngle=3.14159
    g10: ArcOfCircle CenterX=141.022 CenterY=-29.7428 CenterZ=0 NormalX=0 NormalY=0 NormalZ=1 AngleXU=0 Radius=13.75 StartAngle=4.71239 EndAngle=6.28319
    g11: ArcOfCircle CenterX=21.0579 CenterY=-53.2544 CenterZ=0 NormalX=0 NormalY=0 NormalZ=1 AngleXU=0 Radius=12.8879 StartAngle=3.67289 EndAngle=5.2371
    g12: LineSegment StartX=27.5142 StartY=-64.4085 StartZ=0 EndX=24.8842 EndY=-59.8648 EndZ=0
    g13: LineSegment StartX=84.3125 StartY=59.4601 StartZ=0 EndX=84.3125 EndY=64.7101 EndZ=0
    g14: LineSegment StartX=149.522 StartY=46.1101 StartZ=0 EndX=154.772 EndY=46.1101 EndZ=0
    g15: LineSegment StartX=93.9034 StartY=-58.2148 StartZ=0 EndX=93.9034 EndY=-52.9648 EndZ=0
    g16: LineSegment StartX=-3.50636 StartY=-36.8919 StartZ=0 EndX=1.01993 EndY=-34.232 EndZ=0
    g17: LineSegment StartX=-13.5556 StartY=-1.38632 StartZ=0 EndX=-8.30447 EndY=-1.38632 EndZ=0
    g18: LineSegment StartX=-13.5556 StartY=-1.38632 StartZ=0 EndX=-13.5556 EndY=49.1305 EndZ=0
    g19: LineSegment StartX=2.02396 StartY=54.4601 StartZ=0 EndX=84.3125 EndY=54.4601 EndZ=0
    g20: LineSegment StartX=-3.30564 StartY=49.1305 StartZ=0 EndX=-3.30564 EndY=-1.38632 EndZ=0
    g21: LineSegment StartX=144.522 StartY=46.1101 StartZ=0 EndX=144.522 EndY=-29.7428 EndZ=0
    g22: LineSegment StartX=141.022 StartY=-33.2428 StartZ=0 EndX=97.381 EndY=-33.2428 EndZ=0
    g23: LineSegment StartX=97.381 StartY=-33.2428 StartZ=0 EndX=97.381 EndY=-44.4872 EndZ=0
    g24: LineSegment StartX=93.9034 StartY=-47.9648 StartZ=0 EndX=35.4668 EndY=-47.9648 EndZ=0
    g25: LineSegment StartX=35.4668 StartY=-47.9648 StartZ=0 EndX=22.3806 EndY=-55.5396 EndZ=0
    g26: LineSegment StartX=18.7815 StartY=-54.5922 StartZ=0 EndX=5.32855 EndY=-31.6999 EndZ=0
    g27: ArcOfCircle CenterX=59.4385 CenterY=0.0985715 CenterZ=0 NormalX=0 NormalY=0 NormalZ=1 AngleXU=0 Radius=62.7617 StartAngle=3.16525 EndAngle=3.67289
    g28: ArcOfCircle CenterX=84.3125 CenterY=-450.952 CenterZ=0 NormalX=0 NormalY=0 NormalZ=1 AngleXU=0 Radius=505.412 StartAngle=1.46083 EndAngle=1.5708
    g29: ArcOfCircle CenterX=139.192 CenterY=46.1101 CenterZ=0 NormalX=0 NormalY=0 NormalZ=1 AngleXU=0 Radius=5.32961 StartAngle=7e-16 EndAngle=1.46083
    g30: ArcOfCircle CenterX=2.02396 CenterY=49.1305 CenterZ=0 NormalX=0 NormalY=0 NormalZ=1 AngleXU=0 Radius=5.32961 StartAngle=1.5708 EndAngle=3.14159
    g31: LineSegment StartX=84.3125 StartY=54.4601 StartZ=0 EndX=84.3125 EndY=59.4601 EndZ=0
    g32: ArcOfCircle CenterX=21.0579 CenterY=-53.2544 CenterZ=0 NormalX=0 NormalY=0 NormalZ=1 AngleXU=0 Radius=2.64034 StartAngle=3.67289 EndAngle=5.2371
    g33: ArcOfCircle CenterX=93.9034 CenterY=-44.4872 CenterZ=0 NormalX=0 NormalY=0 NormalZ=1 AngleXU=0 Radius=3.47761 StartAngle=4.71239 EndAngle=6.28319
    g34: ArcOfCircle CenterX=141.022 CenterY=-29.7428 CenterZ=0 NormalX=0 NormalY=0 NormalZ=1 AngleXU=0 Radius=3.5 StartAngle=4.71239 EndAngle=6.28319
    g35: LineSegment StartX=93.9034 StartY=-52.9648 StartZ=0 EndX=93.9034 EndY=-47.9648 EndZ=0
    g36: LineSegment StartX=22.3806 StartY=-55.5396 StartZ=0 EndX=24.8842 EndY=-59.8648 EndZ=0
    g37: LineSegment StartX=5.32855 StartY=-31.6999 StartZ=0 EndX=1.01993 EndY=-34.232 EndZ=0
    g38: LineSegment StartX=-3.30564 StartY=-1.38632 StartZ=0 EndX=-8.30447 EndY=-1.38632 EndZ=0
    g39: LineSegment StartX=107.631 StartY=-43.4928 StartZ=0 EndX=107.631 EndY=-44.4872 EndZ=0
    g40: ArcOfCircle CenterX=93.9034 CenterY=-44.4872 CenterZ=0 NormalX=0 NormalY=0 NormalZ=1 AngleXU=0 Radius=13.7276 StartAngle=4.71239 EndAngle=6.28319
  constraints (93):
    c: Horizontal(g0)
    c: Vertical(g1)
    c: Horizontal(g2)
    c: Horizontal(g3)
    c: Coincident(g3,g4)
    c: Parallel(g5,g-13)
    c: Parallel(g-11,g4)
    c: Coincident(g6,g-14)
    c: Coincident(g7,g-4)
    c: Coincident(g8,g-5)
    c: Coincident(g8,g1)
    c: Tangent(g8,g7) = -1.5708
    c: Tangent(g7,g0) = 1.5708
    c: Coincident(g6,g17) = 1.5708
    c: Tangent(g6,g5) = 1.5708
    c: Tangent(g0,g9) = 1.5708
    c: Equal(g8,g9)
    c: Tangent(g2,g10) = 1.5708
    c: Tangent(g1,g10) = 1.5708
    c: Tangent(g5,g11) = 1.5708
    c: Tangent(g4,g11) = 1.5708
    c: Coincident(g11,g-12)
    c: Coincident(g10,g-7)
    c: Coincident(g12,g4)
    c: Coincident(g12,g-12)
    c: Coincident(g13,g-4)
    c: Coincident(g13,g0)
    c: Coincident(g14,g-6)
    c: Coincident(g14,g1)
    c: Horizontal(g14)
    c: Equal(g13,g12)
    c: Coincident(g15,g3)
    c: Coincident(g15,g-10)
    c: Equal(g15,g13)
    c: Coincident(g16,g5)
    c: Coincident(g16,g-14)
    c: Coincident(g17,g-16)
    c: Horizontal(g17)
    c: Coincident(g18,g6)
    c: Vertical(g18)
    c: DistanceY(g13,g13) = 5.25
    c: Tangent(g18,g9) = 1.5708
    c: Horizontal(g19)
    c: Vertical(g20)
    c: Vertical(g21)
    c: Horizontal(g22)
    c: Coincident(g22,g23)
    c: Horizontal(g24)
    c: Coincident(g24,g25)
    c: Parallel(g25,g-11)
    c: Parallel(g26,g-13)
    c: Vertical(g23)
    c: Coincident(g27,g6)
    c: Coincident(g27,g26)
    c: Coincident(g27,g20)
    c: Coincident(g28,g7)
    c: Coincident(g28,g19)
    c: Coincident(g29,g8)
    c: Tangent(g29,g28) = -1.5708
    c: Tangent(g29,g21) = 1.5708
    c: Tangent(g20,g30) = -1.5708
    c: Tangent(g19,g30) = 1.5708
    c: Coincident(g31,g19)
    c: Coincident(g31,g13)
    c: Vertical(g31)
    c: DistanceY(g31,g31) = 5
    c: Coincident(g9,g30)
    c: Tangent(g26,g32) = 1.5708
    c: Tangent(g25,g32) = 1.5708
    c: Tangent(g24,g33) = 1.5708
    c: Tangent(g23,g33) = 1.5708
    c: Tangent(g22,g34) = 1.5708
    c: Tangent(g21,g34) = 1.5708
    c: Coincident(g32,g11)
    c: Coincident(g10,g34)
    c: Coincident(g35,g15)
    c: Coincident(g35,g24)
    c: Coincident(g36,g25)
    c: Coincident(g36,g12)
    c: Coincident(g37,g26)
    c: Coincident(g37,g16)
    c: Perpendicular(g26,g37)
    c: Coincident(g38,g20)
    c: Coincident(g38,g17)
    c: Horizontal(g38)
    c: Equal(g35,g31)
    c: Coincident(g39,g2)
    c: Vertical(g39)
    c: Coincident(g40,g33)
    c: Coincident(g40,g3)
    c: Tangent(g40,g39) = 1.5708
    c: Coincident(g33,g-9)
    c: Vertical(g15)
FEATURE [PartDesign::Pad] Pad013
  Direction = (0,0,1)
  Length = 7.5
  Length2 = 10
  Profile = -> Sketch029
  ReferenceAxis = -> Sketch029 [N_Axis]
  Type = 0
  expr: Length = <<ss_cover>>.cover_thickness
FEATURE [Sketcher::SketchObject] Sketch030
  ExternalGeometry = -> [ShapeBinder004]
  FullyConstrained = true
  MapMode = 5
  Support = -> [XY_Plane021]
  expr: Constraints[37] = Sketch029.Constraints[40]
  expr: Constraints[46] = <<ss_case>>.flange_thickness
  expr: Constraints[76] = <<ss_case>>.flange_thickness
  sketch-geometry (39):
    g0: LineSegment StartX=2.02396 StartY=64.7101 StartZ=0 EndX=84.3125 EndY=64.7101 EndZ=0
    g1: LineSegment StartX=154.772 StartY=46.1101 StartZ=0 EndX=154.772 EndY=-29.7428 EndZ=0
    g2: LineSegment StartX=141.022 StartY=-43.4928 StartZ=0 EndX=107.631 EndY=-43.4928 EndZ=0
    g3: LineSegment StartX=93.9034 StartY=-58.2148 StartZ=0 EndX=38.2145 EndY=-58.2148 EndZ=0
    g4: LineSegment StartX=38.2145 StartY=-58.2148 StartZ=0 EndX=27.5142 EndY=-64.4085 EndZ=0
    g5: LineSegment StartX=9.94659 StartY=-59.7841 StartZ=0 EndX=-3.50636 EndY=-36.8919 EndZ=0
    g6: ArcOfCircle CenterX=59.4385 CenterY=0.0985715 CenterZ=0 NormalX=0 NormalY=0 NormalZ=1 AngleXU=0 Radius=73.0092 StartAngle=3.16193 EndAngle=3.67289
    g7: ArcOfCircle CenterX=84.3125 CenterY=-450.952 CenterZ=0 NormalX=0 NormalY=0 NormalZ=1 AngleXU=0 Radius=515.662 StartAngle=1.46083 EndAngle=1.5708
    g8: ArcOfCircle CenterX=139.192 CenterY=46.1101 CenterZ=0 NormalX=0 NormalY=0 NormalZ=1 AngleXU=0 Radius=15.5796 StartAngle=2e-16 EndAngle=1.46083
    g9: ArcOfCircle CenterX=2.02396 CenterY=49.1305 CenterZ=0 NormalX=0 NormalY=0 NormalZ=1 AngleXU=0 Radius=15.5796 StartAngle=1.5708 EndAngle=3.14159
    g10: ArcOfCircle CenterX=141.022 CenterY=-29.7428 CenterZ=0 NormalX=0 NormalY=0 NormalZ=1 AngleXU=0 Radius=13.75 StartAngle=4.71239 EndAngle=6.28319
    g11: ArcOfCircle CenterX=21.0579 CenterY=-53.2544 CenterZ=0 NormalX=0 NormalY=0 NormalZ=1 AngleXU=0 Radius=12.8879 StartAngle=3.67289 EndAngle=5.2371
    g12: LineSegment StartX=27.5142 StartY=-64.4085 StartZ=0 EndX=24.8842 EndY=-59.8648 EndZ=0
    g13: LineSegment StartX=84.3125 StartY=59.4601 StartZ=0 EndX=84.3125 EndY=64.7101 EndZ=0
    g14: LineSegment StartX=149.522 StartY=46.1101 StartZ=0 EndX=154.772 EndY=46.1101 EndZ=0
    g15: LineSegment StartX=93.9034 StartY=-58.2148 StartZ=0 EndX=93.9034 EndY=-52.9648 EndZ=0
    g16: LineSegment StartX=-3.50636 StartY=-36.8919 StartZ=0 EndX=1.01993 EndY=-34.232 EndZ=0
    g17: LineSegment StartX=-13.5556 StartY=-1.38632 StartZ=0 EndX=-8.30447 EndY=-1.38632 EndZ=0
    g18: LineSegment StartX=-13.5556 StartY=-1.38632 StartZ=0 EndX=-13.5556 EndY=49.1305 EndZ=0
    g19: ArcOfCircle CenterX=141.022 CenterY=-29.7428 CenterZ=0 NormalX=0 NormalY=0 NormalZ=1 AngleXU=0 Radius=11.75 StartAngle=4.71239 EndAngle=6.28319
    g20: LineSegment StartX=152.772 StartY=-29.7428 StartZ=0 EndX=154.772 EndY=-29.7428 EndZ=0
    g21: LineSegment StartX=152.772 StartY=-29.7428 StartZ=0 EndX=152.772 EndY=46.1101 EndZ=0
    g22: ArcOfCircle CenterX=93.9034 CenterY=-44.4872 CenterZ=0 NormalX=0 NormalY=0 NormalZ=1 AngleXU=0 Radius=11.7276 StartAngle=4.71239 EndAngle=6.28319
    g23: LineSegment StartX=105.631 StartY=-44.4872 StartZ=0 EndX=105.631 EndY=-41.4928 EndZ=0
    g24: LineSegment StartX=105.631 StartY=-41.4928 StartZ=0 EndX=141.022 EndY=-41.4928 EndZ=0
    g25: LineSegment StartX=93.9034 StartY=-56.2148 StartZ=0 EndX=37.6774 EndY=-56.2148 EndZ=0
    g26: LineSegment StartX=37.6774 StartY=-56.2148 StartZ=0 EndX=26.5123 EndY=-62.6775 EndZ=0
    g27: ArcOfCircle CenterX=21.0579 CenterY=-53.2544 CenterZ=0 NormalX=0 NormalY=0 NormalZ=1 AngleXU=0 Radius=10.8879 StartAngle=3.67289 EndAngle=5.2371
    g28: LineSegment StartX=11.6709 StartY=-58.7708 StartZ=0 EndX=-1.78206 EndY=-35.8786 EndZ=0
    g29: LineSegment StartX=107.631 StartY=-43.4928 StartZ=0 EndX=107.631 EndY=-44.4872 EndZ=0
    g30: ArcOfCircle CenterX=93.9034 CenterY=-44.4872 CenterZ=0 NormalX=0 NormalY=0 NormalZ=1 AngleXU=0 Radius=13.7276 StartAngle=4.71239 EndAngle=6.28319
    g31: LineSegment StartX=107.631 StartY=-44.4872 StartZ=0 EndX=102.381 EndY=-44.4872 EndZ=0
    g32: LineSegment StartX=11.6709 StartY=-58.7708 StartZ=0 EndX=9.94659 EndY=-59.7841 EndZ=0
    g33: ArcOfCircle CenterX=59.4385 CenterY=0.0985715 CenterZ=0 NormalX=0 NormalY=0 NormalZ=1 AngleXU=0 Radius=71.0092 StartAngle=3.16251 EndAngle=3.67289
    g34: LineSegment StartX=-11.5552 StartY=-1.38632 StartZ=0 EndX=-11.5552 EndY=49.1305 EndZ=0
    g35: LineSegment StartX=2.02389 StartY=62.7097 StartZ=0 EndX=84.3125 EndY=62.7101 EndZ=0
    g36: ArcOfCircle CenterX=2.02396 CenterY=49.1305 CenterZ=0 NormalX=0 NormalY=0 NormalZ=1 AngleXU=0 Radius=13.5792 StartAngle=1.5708 EndAngle=3.14159
    g37: ArcOfCircle CenterX=84.3125 CenterY=-450.952 CenterZ=0 NormalX=0 NormalY=0 NormalZ=1 AngleXU=0 Radius=513.662 StartAngle=1.46083 EndAngle=1.5708
    g38: ArcOfCircle CenterX=139.192 CenterY=46.1101 CenterZ=0 NormalX=0 NormalY=0 NormalZ=1 AngleXU=0 Radius=13.5796 StartAngle=-1.8e-15 EndAngle=1.46083
  constraints (95):
    c: Horizontal(g0)
    c: Vertical(g1)
    c: Horizontal(g2)
    c: Horizontal(g3)
    c: Coincident(g3,g4)
    c: Parallel(g5,g-13)
    c: Parallel(g-11,g4)
    c: Coincident(g6,g-14)
    c: Coincident(g7,g-4)
    c: Coincident(g8,g1)
    c: Tangent(g8,g7) = -1.5708
    c: Tangent(g7,g0) = 1.5708
    c: Coincident(g6,g17) = 1.5708
    c: Tangent(g6,g5) = 1.5708
    c: Tangent(g0,g9) = 1.5708
    c: Equal(g8,g9)
    c: Tangent(g2,g10) = 1.5708
    c: Tangent(g1,g10) = 1.5708
    c: Tangent(g5,g11) = 1.5708
    c: Tangent(g4,g11) = 1.5708
    c: Coincident(g12,g4)
    c: Coincident(g12,g-12)
    c: Coincident(g13,g-4)
    c: Coincident(g13,g0)
    c: Coincident(g14,g-6)
    c: Coincident(g14,g1)
    c: Horizontal(g14)
    c: Equal(g13,g12)
    c: Coincident(g15,g3)
    c: Coincident(g15,g-10)
    c: Equal(g15,g13)
    c: Coincident(g16,g5)
    c: Coincident(g16,g-14)
    c: Coincident(g17,g-16)
    c: Horizontal(g17)
    c: Coincident(g18,g6)
    c: Vertical(g18)
    c: DistanceY(g13,g13) = 5.25
    c: Tangent(g18,g9) = 1.5708
    c: Coincident(g-5,g8)
    c: Coincident(g11,g-12)
    c: Coincident(g10,g-7)
    c: Coincident(g19,g10)
    c: Coincident(g20,g19)
    c: Coincident(g20,g1)
    c: Horizontal(g20)
    c: DistanceX(g20,g20) = 2
    c: Coincident(g21,g19)
    c: PointOnObject(g21,g14)
    c: Vertical(g21)
    c: PointOnObject(g22,g15)
    c: Coincident(g24,g23)
    c: Horizontal(g24)
    c: Tangent(g23,g22) = -1.5708
    c: Horizontal(g25)
    c: Coincident(g26,g25)
    c: PointOnObject(g26,g12)
    c: Coincident(g27,g11)
    c: Coincident(g27,g26)
    c: Coincident(g28,g27)
    c: PointOnObject(g28,g16)
    c: Parallel(g28,g-13)
    c: Parallel(g26,g-11)
    c: Tangent(g24,g19) = -1.5708
    c: Coincident(g29,g2)
    c: Vertical(g29)
    c: Coincident(g30,g22)
    c: Coincident(g30,g3)
    c: Coincident(g30,g29)
    c: Vertical(g15)
    c: Horizontal(g29,g-9)
    c: Tangent(g25,g22) = 1.5708
    c: Horizontal(g22,g-9)
    c: Coincident(g31,g29)
    c: Coincident(g31,g-9)
    c: Equal(g31,g15)
    c: DistanceX(g22,g29) = 2
    c: Coincident(g32,g27)
    c: Coincident(g32,g5)
    c: Perpendicular(g32,g28)
    c: Equal(g32,g20)
    c: Coincident(g33,g6)
    c: Coincident(g33,g28)
    c: Coincident(g34,g33)
    c: PointOnObject(g35,g13)
    c: Tangent(g34,g36) = 1.5708
    c: Tangent(g35,g36) = 1.5708
    c: Coincident(g36,g9)
    c: Vertical(g34)
    c: PointOnObject(g33,g17)
    c: Coincident(g37,g7)
    c: Coincident(g37,g35)
    c: Coincident(g38,g8)
    c: Coincident(g38,g21)
    c: Tangent(g38,g37) = -1.5708
FEATURE [PartDesign::Pocket] Pocket008
  BaseFeature = -> Pad013
  Direction = (0,0,-1)
  Length = 1.5
  Length2 = 5
  Profile = -> Sketch030
  ReferenceAxis = -> Sketch030 [N_Axis]
  Reversed = true
  Type = 0
  expr: Length = <<ss_case>>.flange_thickness - <<ss_cover>>.shadow_gap
FEATURE [Sketcher::SketchObject] Sketch031
  ExternalGeometry = -> [ShapeBinder004]
  FullyConstrained = true
  MapMode = 5
  Support = -> [XY_Plane021]
  expr: Constraints[10] = <<ss_case>>.threaded_insert_hole_od
  sketch-geometry (12):
    g0: Circle CenterX=-6.70447 CenterY=-1.38632 CenterZ=0 NormalX=0 NormalY=0 NormalZ=1 AngleXU=0 Radius=2
    g1: Circle CenterX=19.5209 CenterY=-59.0934 CenterZ=0 NormalX=0 NormalY=0 NormalZ=1 AngleXU=0 Radius=2
    g2: Circle CenterX=98.7666 CenterY=-49.3504 CenterZ=0 NormalX=0 NormalY=0 NormalZ=1 AngleXU=0 Radius=2
    g3: Circle CenterX=145.901 CenterY=-34.6219 CenterZ=0 NormalX=0 NormalY=0 NormalZ=1 AngleXU=0 Radius=2
    g4: Circle CenterX=145.695 CenterY=51.9344 CenterZ=0 NormalX=0 NormalY=0 NormalZ=1 AngleXU=0 Radius=2
    g5: Circle CenterX=-3.86479 CenterY=55.0204 CenterZ=0 NormalX=0 NormalY=0 NormalZ=1 AngleXU=0 Radius=2
    g6: LineSegment StartX=-8.30447 StartY=-1.38632 StartZ=0 EndX=-8.30447 EndY=49.1305 EndZ=0
    g7: LineSegment StartX=2.02513 StartY=59.4601 StartZ=0 EndX=27.7344 EndY=59.4601 EndZ=0
    g8: ArcOfCircle CenterX=2.02513 CenterY=49.1305 CenterZ=0 NormalX=0 NormalY=0 NormalZ=1 AngleXU=0 Radius=10.3296 StartAngle=1.5708 EndAngle=3.14159
    g9: LineSegment StartX=2.02513 StartY=49.1305 StartZ=0 EndX=-5.279 EndY=56.4346 EndZ=0
    g10: LineSegment StartX=-5.279 StartY=56.4346 StartZ=0 EndX=2.02513 EndY=59.4601 EndZ=0
    g11: LineSegment StartX=-5.279 StartY=56.4346 StartZ=0 EndX=-8.30447 EndY=49.1305 EndZ=0
  constraints (27):
    c: Coincident(g0,g-3)
    c: Coincident(g1,g-4)
    c: Coincident(g2,g-5)
    c: Coincident(g3,g-6)
    c: Coincident(g4,g-7)
    c: Equal(g5,g0)
    c: Equal(g0,g1)
    c: Equal(g1,g2)
    c: Equal(g2,g3)
    c: Equal(g3,g4)
    c: Diameter(g5) = 4
    c: Coincident(g6,g-9)
    c: Coincident(g7,g-8)
    c: Horizontal(g7)
    c: Vertical(g6)
    c: Tangent(g6,g8) = 1.5708
    c: Tangent(g7,g8) = 1.5708
    c: Equal(g-10,g8)
    c: Coincident(g9,g8)
    c: PointOnObject(g9,g8)
    c: Coincident(g10,g9)
    c: Coincident(g10,g7)
    c: Coincident(g11,g9)
    c: Coincident(g11,g6)
    c: Equal(g11,g10)
    c: PointOnObject(g5,g9)
    c: PointOnObject(g9,g5)
FEATURE [PartDesign::Hole] Hole001
  BaseFeature = -> Pocket008
  CustomThreadClearance = 0
  Depth = 5
  DepthType = 0
  Diameter = 4
  DrillForDepth = false
  DrillPoint = 0
  DrillPointAngle = 118
  HoleCutCountersinkAngle = 90
  HoleCutCustomValues = false
  HoleCutDepth = 0
  HoleCutDiameter = 6.1
  HoleCutType = 0
  ModelThread = false
  Profile = -> Sketch031
  Reversed = true
  Tapered = false
  TaperedAngle = 90
  ThreadClass = 0
  ThreadDepth = 5
  ThreadDepthType = 0
  ThreadDirection = 0
  ThreadFit = 0
  ThreadSize = 0
  ThreadType = 0
  Threaded = false
  UseCustomThreadClearance = false
  expr: Depth = <<ss_case>>.flange_thickness + <<ss_case>>.threaded_insert_thickness
  expr: Diameter = <<ss_case>>.threaded_insert_hole_od
FEATURE [PartDesign::Fillet] Fillet
  Base = -> Hole001 [Edge47,Edge48,Edge49,Edge7,Edge4,Edge10,Edge38,Edge39,Edge40,Edge41,Edge43,Edge44,Edge45,Edge46]
  BaseFeature = -> Hole001
  Radius = 6
  SupportTransform = false
  UseAllEdges = false
FEATURE [PartDesign::Body] Body008  label="b_cover"
  Group = -> [ShapeBinder004,Sketch029,Pad013,Sketch030,Pocket008,Sketch031,Hole001,Fillet]
  Origin = -> Origin021
  Tip = -> Fillet
COMPONENT P9 — recipe-attached ("front_tenting", modeled in this document).
Construction recipe (the document's own serialized feature program — sketch geometry with constraints, then the solid features built on it; lengths are millimeters unless a unit is written):

FEATURE [PartDesign::ShapeBinder] ShapeBinder005
  Support = -> [Pad005]
  TraceSupport = false
FEATURE [Sketcher::SketchObject] Sketch032
  ExternalGeometry = -> [ShapeBinder005]
  FullyConstrained = true
  MapMode = 5
  Support = -> [XY_Plane023]
  expr: Constraints[13] = <<ss_tenting>>.leg_diameter
  sketch-geometry (25):
    g0: LineSegment StartX=-8.30447 StartY=-1.38632 StartZ=0 EndX=-8.30447 EndY=49.1305 EndZ=0
    g1: LineSegment StartX=2.02513 StartY=59.4601 StartZ=0 EndX=27.7344 EndY=59.4601 EndZ=0
    g2: ArcOfCircle CenterX=2.02513 CenterY=49.1305 CenterZ=0 NormalX=0 NormalY=0 NormalZ=1 AngleXU=0 Radius=10.3296 StartAngle=1.5708 EndAngle=3.14159
    g3: LineSegment StartX=2.02513 StartY=49.1305 StartZ=0 EndX=-3.13967 EndY=54.2953 EndZ=0
    g4: Circle CenterX=-4.14763 CenterY=55.3033 CenterZ=0 NormalX=0 NormalY=0 NormalZ=1 AngleXU=0 Radius=1.6
    g5: Circle CenterX=-4.14763 CenterY=55.3033 CenterZ=0 NormalX=0 NormalY=0 NormalZ=1 AngleXU=0 Radius=5
    g6: Circle CenterX=-6.70447 CenterY=-1.38632 CenterZ=0 NormalX=0 NormalY=0 NormalZ=1 AngleXU=0 Radius=5
    g7: LineSegment StartX=-11.7045 StartY=-1.38632 StartZ=0 EndX=-11.7045 EndY=52.7464 EndZ=0
    g8: ArcOfCircle CenterX=-4.14763 CenterY=52.7464 CenterZ=0 NormalX=0 NormalY=0 NormalZ=1 AngleXU=0 Radius=7.55684 StartAngle=1.5708 EndAngle=3.14159
    g9: LineSegment StartX=-1.70447 StartY=-1.38632 StartZ=0 EndX=-1.70447 EndY=49.1305 EndZ=0
    g10: ArcOfCircle CenterX=-4.14763 CenterY=55.3033 CenterZ=0 NormalX=0 NormalY=0 NormalZ=1 AngleXU=0 Radius=5 StartAngle=5.49779 EndAngle=7.85398
    g11: ArcOfCircle CenterX=2.02513 CenterY=49.1305 CenterZ=0 NormalX=0 NormalY=0 NormalZ=1 AngleXU=0 Radius=3.72961 StartAngle=2.35619 EndAngle=3.14159
    g12: Circle CenterX=-6.70447 CenterY=-1.38632 CenterZ=0 NormalX=0 NormalY=0 NormalZ=1 AngleXU=0 Radius=1.6
    g13: Circle CenterX=-4.14763 CenterY=55.3033 CenterZ=0 NormalX=0 NormalY=0 NormalZ=1 AngleXU=0 Radius=1.6
    g14: Circle CenterX=19.5209 CenterY=-59.0934 CenterZ=0 NormalX=0 NormalY=0 NormalZ=1 AngleXU=0 Radius=5
    g15: ArcOfCircle CenterX=59.4385 CenterY=0.0985715 CenterZ=0 NormalX=0 NormalY=0 NormalZ=1 AngleXU=0 Radius=71.1585 StartAngle=3.16246 EndAngle=3.67289
    g16: ArcOfCircle CenterX=59.4385 CenterY=0.0985715 CenterZ=0 NormalX=0 NormalY=0 NormalZ=1 AngleXU=0 Radius=61.161 StartAngle=3.16587 EndAngle=3.67289
    g17: LineSegment StartX=6.7086 StartY=-30.8889 StartZ=0 EndX=19.6569 EndY=-52.9224 EndZ=0
    g18: LineSegment StartX=-1.91071 StartY=-35.9542 StartZ=0 EndX=6.7086 EndY=-30.8889 EndZ=0
    g19: LineSegment StartX=-1.91071 StartY=-35.9542 StartZ=0 EndX=12.8097 EndY=-61.0033 EndZ=0
    g20: ArcOfCircle CenterX=18.6324 CenterY=-57.5815 CenterZ=0 NormalX=0 NormalY=0 NormalZ=1 AngleXU=0 Radius=6.75363 StartAngle=3.67289 EndAngle=5.24369
    g21: LineSegment StartX=19.5209 StartY=-59.0934 StartZ=0 EndX=22.0541 EndY=-63.4041 EndZ=0
    g22: ArcOfCircle CenterX=22.8724 CenterY=-51.0328 CenterZ=0 NormalX=0 NormalY=0 NormalZ=1 AngleXU=0 Radius=3.72961 StartAngle=3.67289 EndAngle=4.31835
    g23: ArcOfCircle CenterX=19.5209 CenterY=-59.0934 CenterZ=0 NormalX=0 NormalY=0 NormalZ=1 AngleXU=0 Radius=5 StartAngle=5.24369 EndAngle=7.45994
    g24: Circle CenterX=19.5209 CenterY=-59.0934 CenterZ=0 NormalX=0 NormalY=0 NormalZ=1 AngleXU=0 Radius=1.6
  constraints (60):
    c: Coincident(g-3,g0)
    c: Coincident(g1,g-4)
    c: Horizontal(g1)
    c: Vertical(g0)
    c: Tangent(g0,g2) = 1.5708
    c: Tangent(g1,g2) = 1.5708
    c: Equal(g-5,g2)
    c: Coincident(g3,g2)
    c: Symmetric(g0,g1,g3)
    c: PointOnObject(g4,g3)
    c: Tangent(g4,g2)
    c: Equal(g-6,g4)
    c: Coincident(g5,g4)
    c: Diameter(g5) = 10
    c: Coincident(g6,g-6)
    c: Equal(g6,g5)
    c: PointOnObject(g7,g6)
    c: Vertical(g7)
    c: Tangent(g8,g5) = -1.5708
    c: Tangent(g8,g7) = 1.5708
    c: Vertical(g5,g8)
    c: Coincident(g10,g4)
    c: Coincident(g10,g8)
    c: Tangent(g9,g11) = 1.5708
    c: Tangent(g10,g11) = 1.5708
    c: Coincident(g11,g2)
    c: Coincident(g13,g10)
    c: Equal(g13,g12)
    c: Equal(g12,g-6)
    c: Coincident(g14,g-7)
    c: Equal(g14,g6)
    c: Coincident(g15,g-8)
    c: Coincident(g15,g7)
    c: Coincident(g16,g15)
    c: Coincident(g16,g9)
    c: Coincident(g17,g16)
    c: Coincident(g18,g15)
    c: Coincident(g18,g16)
    c: PointOnObject(g-8,g18)
    c: PointOnObject(g9,g6)
    c: Coincident(g19,g15)
    c: Tangent(g20,g19) = -1.5708
    c: Parallel(g19,g-9)
    c: Coincident(g21,g14)
    c: PointOnObject(g21,g14)
    c: Parallel(g21,g-9)
    c: Coincident(g20,g21)
    c: Parallel(g17,g-9)
    c: Coincident(g23,g14)
    c: Coincident(g23,g20)
    c: Tangent(g23,g22) = 1.5708
    c: Tangent(g22,g17) = -1.5708
    c: Perpendicular(g17,g18)
    c: Horizontal(g12,g9)
    c: Coincident(g12,g6)
    c: Perpendicular(g20,g21)
    c: Equal(g11,g22)
    c: Horizontal(g7,g12)
    c: Coincident(g24,g23)
    c: Equal(g24,g12)
FEATURE [PartDesign::Pad] Pad014
  Direction = (0,0,1)
  Length = 50
  Length2 = 10
  Profile = -> Sketch032
  ReferenceAxis = -> Sketch032 [N_Axis]
  Reversed = true
  Type = 0
FEATURE [Sketcher::SketchObject] Sketch033
  ExternalGeometry = -> [ShapeBinder005]
  FullyConstrained = true
  MapMode = 5
  Support = -> [XY_Plane023]
  expr: Constraints[2] = <<ss_case>>.wall_offset
  sketch-geometry (7):
    g0: LineSegment StartX=149.522 StartY=-29.7428 StartZ=0 EndX=154.772 EndY=-29.7428 EndZ=0
    g1: LineSegment StartX=141.022 StartY=-38.2428 StartZ=0 EndX=141.022 EndY=-43.4928 EndZ=0
    g2: ArcOfCircle CenterX=141.022 CenterY=-29.7428 CenterZ=0 NormalX=0 NormalY=0 NormalZ=1 AngleXU=0 Radius=13.75 StartAngle=4.71239 EndAngle=6.28319
    g3: LineSegment StartX=141.022 StartY=-29.7428 StartZ=0 EndX=150.744 EndY=-39.4656 EndZ=0
    g4: LineSegment StartX=150.744 StartY=-39.4656 StartZ=0 EndX=154.772 EndY=-29.7428 EndZ=0
    g5: LineSegment StartX=150.744 StartY=-39.4656 StartZ=0 EndX=141.022 EndY=-43.4928 EndZ=0
    g6: Circle CenterX=150.744 CenterY=-39.4656 CenterZ=0 NormalX=0 NormalY=0 NormalZ=1 AngleXU=0 Radius=10.5238
  constraints (17):
    c: Coincident(g0,g-4)
    c: Horizontal(g0)
    c: DistanceX(g0,g0) = 5.25
    c: Coincident(g1,g-4)
    c: Vertical(g1)
    c: Coincident(g2,g-4)
    c: Coincident(g2,g0)
    c: Coincident(g2,g1)
    c: Coincident(g3,g2)
    c: PointOnObject(g3,g2)
    c: Coincident(g4,g3)
    c: Coincident(g4,g0)
    c: Coincident(g5,g3)
    c: Coincident(g5,g1)
    c: Equal(g5,g4)
    c: Coincident(g6,g3)
    c: PointOnObject(g1,g6)
FEATURE [PartDesign::Plane] DatumPlane003
  AttachmentOffset = pos=(0,0,0) rot=(-0.706244,0.706244,0.049385;0.197381rad)
  Length = 89.1612
  MapMode = 11
  Placement = pos=(150.744,-39.4656,0) rot=(-0.137845,0,0.990454;1.59017rad)
  ResizeMode = 0
  Support = -> [Sketch033]
  Width = 199.043
  expr: .AttachmentOffset.Rotation.Pitch = <<ss_tenting>>.yaw
  expr: .AttachmentOffset.Rotation.Roll = -<<ss_tenting>>.pitch
FEATURE [Sketcher::SketchObject] Sketch034
  ExternalGeometry = -> [ShapeBinder005]
  FullyConstrained = true
  MapMode = 5
  Placement = pos=(150.744,-39.4656,2e-16) rot=(-0.137845,0,0.990454;1.59017rad)
  Support = -> [DatumPlane003]
  sketch-geometry (4):
    g0: LineSegment StartX=-63.6547 StartY=203.285 StartZ=0 EndX=147.963 EndY=203.285 EndZ=0
    g1: LineSegment StartX=147.963 StartY=203.285 StartZ=0 EndX=147.963 EndY=-50.4467 EndZ=0
    g2: LineSegment StartX=147.963 StartY=-50.4467 StartZ=0 EndX=-63.6547 EndY=-50.4467 EndZ=0
    g3: LineSegment StartX=-63.6547 StartY=-50.4467 StartZ=0 EndX=-63.6547 EndY=203.285 EndZ=0
  constraints (12):
    c: Coincident(g0,g1)
    c: Coincident(g1,g2)
    c: Coincident(g2,g3)
    c: Coincident(g3,g0)
    c: Horizontal(g0)
    c: Horizontal(g2)
    c: Vertical(g1)
    c: Vertical(g3)
    c: DistanceX(g2,g-6) = 50
    c: DistanceX(g-5,g1) = 50
    c: DistanceY(g1,g-4) = 50
    c: DistanceY(g-3,g0) = 50
FEATURE [PartDesign::Pocket] Pocket009
  BaseFeature = -> Pad014
  Direction = (0.139173,-0.137819,-0.980631)
  Length = 5
  Length2 = 5
  Profile = -> Sketch034
  ReferenceAxis = -> Sketch034 [N_Axis]
  Type = 1
FEATURE [Sketcher::SketchObject] Sketch035
  FullyConstrained = true
  MapMode = 5
  Placement = pos=(150.744,-39.4656,2e-16) rot=(-0.137845,0,0.990454;1.59017rad)
  Support = -> [DatumPlane003]
FEATURE [PartDesign::Plane] DatumPlane004
  AttachmentOffset = pos=(0,0,6.1) rot=(0,0,1;0rad)
  Length = 60
  MapMode = 5
  Placement = pos=(0,0,-6.1) rot=(0,1,0;3.14159rad)
  ResizeMode = 0
  Support = -> [XY_Plane023]
  Width = 60
  expr: .AttachmentOffset.Base.z = <<ss_tenting>>.head_offset
FEATURE [Sketcher::SketchObject] Sketch036
  ExternalGeometry = -> [Sketch032,ShapeBinder005]
  FullyConstrained = true
  MapMode = 5
  Placement = pos=(0,0,-6.1) rot=(0,1,0;3.14159rad)
  Support = -> [DatumPlane004]
  expr: Constraints[5] = <<ss_case>>.screw_head_od + 0.4
  sketch-geometry (3):
    g0: Circle CenterX=-19.5209 CenterY=-59.0934 CenterZ=0 NormalX=0 NormalY=0 NormalZ=1 AngleXU=0 Radius=2.95
    g1: Circle CenterX=6.70447 CenterY=-1.38632 CenterZ=0 NormalX=0 NormalY=0 NormalZ=1 AngleXU=0 Radius=2.95
    g2: Circle CenterX=4.14763 CenterY=55.3033 CenterZ=0 NormalX=0 NormalY=0 NormalZ=1 AngleXU=0 Radius=2.95
  constraints (6):
    c: Coincident(g0,g-5)
    c: Coincident(g1,g-4)
    c: Coincident(g2,g-3)
    c: Equal(g0,g1)
    c: Equal(g1,g2)
    c: Diameter(g2) = 5.9
FEATURE [PartDesign::Pocket] Pocket010
  BaseFeature = -> Pocket009
  Direction = (0,0,1)
  Length = 5
  Length2 = 5
  Profile = -> Sketch036
  ReferenceAxis = -> Sketch036 [N_Axis]
  Reversed = true
  Type = 1
FEATURE [PartDesign::Body] Body009  label="p_front_tent"
  Group = -> [ShapeBinder005,Sketch032,Pad014,Sketch033,DatumPlane003,Sketch034,Pocket009,Sketch035,DatumPlane004,Sketch036,Pocket010]
  Origin = -> Origin023
  Tip = -> Pocket010
FEATURE [PartDesign::ShapeBinder] ShapeBinder006
  Support = -> [Pad005]
  TraceSupport = false
FEATURE [Sketcher::SketchObject] Sketch037
  ExternalGeometry = -> [ShapeBinder006]
  FullyConstrained = true
  MapMode = 5
  Support = -> [XY_Plane024]
  expr: Constraints[3] = <<ss_case>>.wall_offset
  sketch-geometry (4):
    g0: LineSegment StartX=147.032 StartY=-35.7533 StartZ=0 EndX=150.744 EndY=-39.4656 EndZ=0
    g1: Circle CenterX=150.744 CenterY=-39.4656 CenterZ=0 NormalX=0 NormalY=0 NormalZ=1 AngleXU=0 Radius=5.25
    g2: LineSegment StartX=147.032 StartY=-35.7533 StartZ=0 EndX=149.522 EndY=-29.7429 EndZ=0
    g3: LineSegment StartX=147.032 StartY=-35.7533 StartZ=0 EndX=141.022 EndY=-38.2428 EndZ=0
  constraints (10):
    c: PointOnObject(g0,g-3)
    c: Coincident(g1,g0)
    c: PointOnObject(g0,g1)
    c: Radius(g1) = 5.25
    c: Perpendicular(g-3,g0)
    c: Coincident(g2,g0)
    c: Coincident(g2,g-3)
    c: Coincident(g3,g2)
    c: Coincident(g3,g-3)
    c: Equal(g2,g3)
FEATURE [PartDesign::Plane] DatumPlane005
  AttachmentOffset = pos=(0,0,0) rot=(-0.706244,0.706244,0.049385;0.197381rad)
  Length = 89.1612
  MapMode = 11
  Placement = pos=(150.744,-39.4656,0) rot=(-0.137845,0,0.990454;1.59017rad)
  ResizeMode = 0
  Support = -> [Sketch037]
  Width = 199.043
  expr: .AttachmentOffset.Rotation.Pitch = <<ss_tenting>>.yaw
  expr: .AttachmentOffset.Rotation.Roll = -<<ss_tenting>>.pitch
FEATURE [PartDesign::Plane] DatumPlane006
  AttachmentOffset = pos=(0,0,6.1) rot=(0,0,1;0rad)
  Length = 60
  MapMode = 5
  Placement = pos=(0,0,-6.1) rot=(0,1,0;3.14159rad)
  ResizeMode = 0
  Support = -> [XY_Plane024]
  Width = 60
  expr: .AttachmentOffset.Base.z = <<ss_tenting>>.head_offset
FEATURE [Sketcher::SketchObject] Sketch038
  ExternalGeometry = -> [ShapeBinder006]
  FullyConstrained = true
  MapMode = 5
  Support = -> [XY_Plane024]
  expr: Constraints[3] = <<ss_tenting>>.leg_diameter
  sketch-geometry (2):
    g0: Circle CenterX=145.695 CenterY=51.9344 CenterZ=0 NormalX=0 NormalY=0 NormalZ=1 AngleXU=0 Radius=5
    g1: Circle CenterX=145.695 CenterY=51.9344 CenterZ=0 NormalX=0 NormalY=0 NormalZ=1 AngleXU=0 Radius=1.6
  constraints (4):
    c: Coincident(g0,g-3)
    c: Coincident(g1,g0)
    c: Equal(g-3,g1)
    c: Diameter(g0) = 10
FEATURE [PartDesign::Pad] Pad015
  Direction = (0,0,1)
  Length = 50
  Length2 = 10
  Profile = -> Sketch038
  ReferenceAxis = -> Sketch038 [N_Axis]
  Reversed = true
  Type = 0
FEATURE [Sketcher::SketchObject] Sketch039
  ExternalGeometry = -> [ShapeBinder006,Pad015]
  FullyConstrained = true
  MapMode = 5
  Placement = pos=(150.744,-39.4656,2e-16) rot=(-0.137845,0,0.990454;1.59017rad)
  Support = -> [DatumPlane005]
  sketch-geometry (1):
    g0: Circle CenterX=90.5104 CenterY=3.23019 CenterZ=0 NormalX=0 NormalY=0 NormalZ=1 AngleXU=0 Radius=25
  constraints (2):
    c: Coincident(g0,g-4)
    c: Diameter(g0) = 50
FEATURE [PartDesign::Pocket] Pocket011
  BaseFeature = -> Pad015
  Direction = (0.139173,-0.137819,-0.980631)
  Length = 5
  Length2 = 5
  Profile = -> Sketch039
  ReferenceAxis = -> Sketch039 [N_Axis]
  Type = 1
FEATURE [Sketcher::SketchObject] Sketch040
  ExternalGeometry = -> [ShapeBinder006]
  FullyConstrained = true
  MapMode = 5
  Placement = pos=(0,0,-6.1) rot=(0,1,0;3.14159rad)
  Support = -> [DatumPlane006]
  expr: Constraints[1] = <<ss_case>>.screw_head_od + 0.4
  sketch-geometry (1):
    g0: Circle CenterX=-145.695 CenterY=51.9344 CenterZ=0 NormalX=0 NormalY=0 NormalZ=1 AngleXU=0 Radius=2.95
  constraints (2):
    c: Coincident(g0,g-3)
    c: Diameter(g0) = 5.9
FEATURE [PartDesign::Pocket] Pocket012
  BaseFeature = -> Pocket011
  Direction = (0,0,1)
  Length = 5
  Length2 = 5
  Profile = -> Sketch040
  ReferenceAxis = -> Sketch040 [N_Axis]
  Reversed = true
  Type = 1
FEATURE [PartDesign::Body] Body010  label="p_rear_tent"
  Group = -> [ShapeBinder006,Sketch037,DatumPlane005,DatumPlane006,Sketch038,Pad015,Sketch039,Pocket011,Sketch040,Pocket012]
  Origin = -> Origin024
  Tip = -> Pocket012
PROVENANCE & LICENSES
A FreeCAD (.FCStd) document from a public repository crawl; recipes are the document's own serialized feature recipes (and, for linked parts, companion documents' recipes).
License: as declared in the source repository (recorded in the dataset sidecar).
